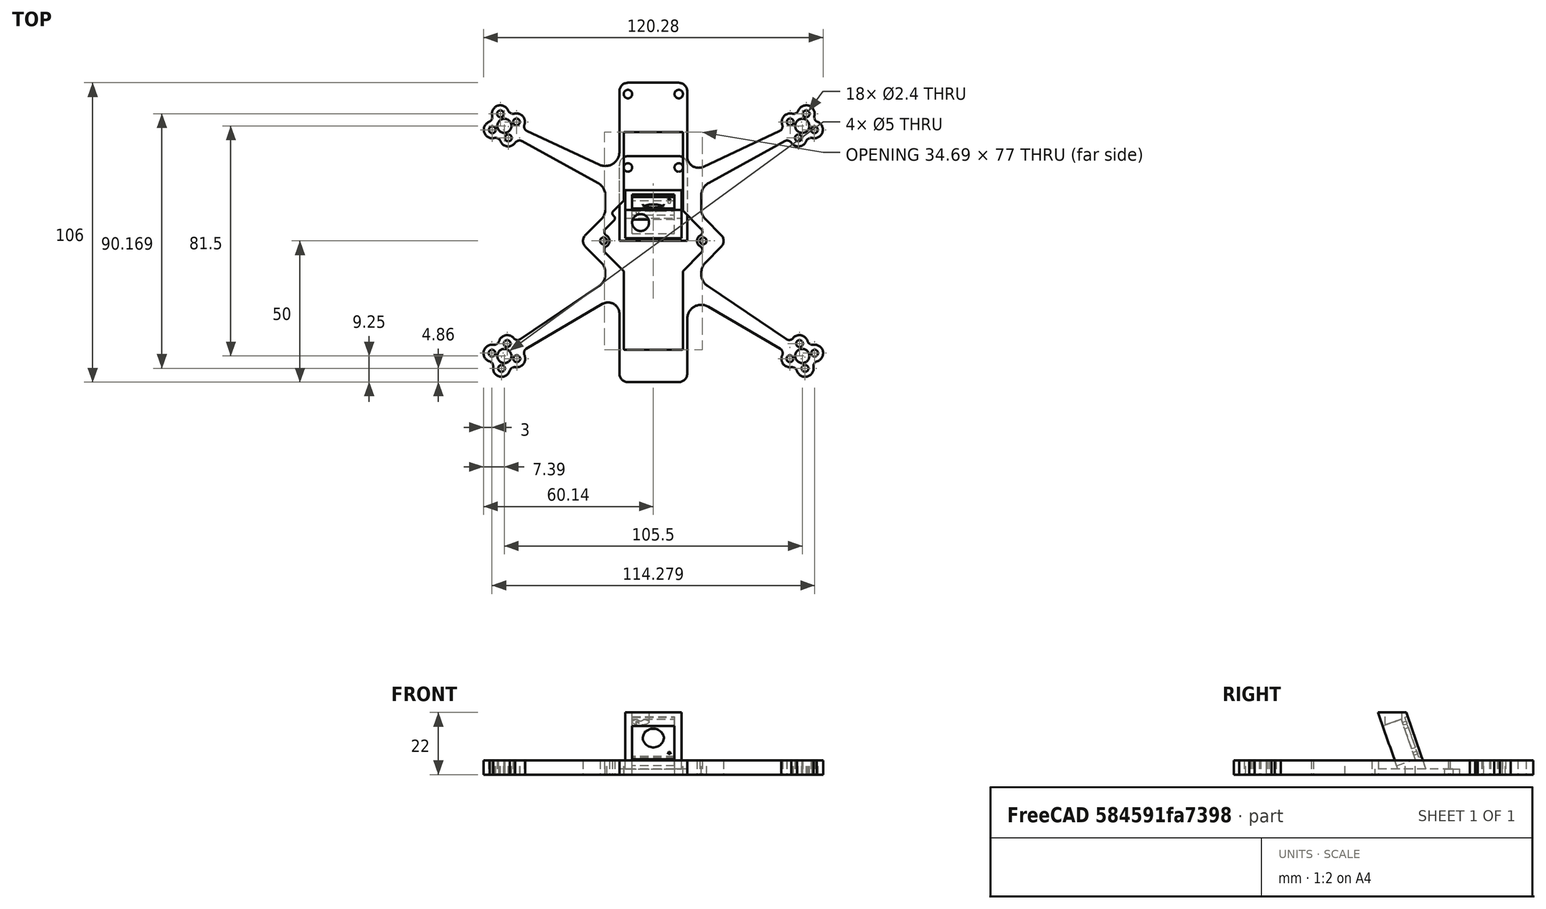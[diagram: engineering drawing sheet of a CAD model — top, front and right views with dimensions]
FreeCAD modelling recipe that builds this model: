
FCSTD DOCUMENT  (FreeCAD 0.19R)
Label: board_outline
License: All rights reserved
LicenseURL: http://en.wikipedia.org/wiki/All_rights_reserved
objects: Sketcher::SketchObject×10, PartDesign::Pocket×5, PartDesign::Pad×2, PartDesign::Body×2, Fem::FemSolverObjectPython×1, Fem::FemMeshObjectPython×1, App::MaterialObjectPython×1, Fem::ConstraintFixed×1, Fem::ConstraintForce×1, Fem::FemAnalysis×1, Spreadsheet::Sheet×1, PartDesign::AdditiveLoft×1
note: 28 computed .brp shape members not serialized (recipe doc carries the construction recipe); baked Part::Feature solids carry a one-line shape summary decoded from their .brp

FEATURE [Sketcher::SketchObject] Sketch  label="Right Half"
  FullyConstrained = true
  MapMode = 5
  Support = -> [XY_Plane]
  expr: Constraints[0] = Spreadsheet.PropDiameter
  sketch-geometry (208):
    g0: Circle CenterX=52.75 CenterY=40.75 CenterZ=0 NormalX=0 NormalY=0 NormalZ=1 AngleXU=0 Radius=38.25
    g1: LineSegment StartX=0 StartY=40.75 StartZ=0 EndX=52.75 EndY=40.75 EndZ=0
    g2: LineSegment StartX=52.75 StartY=40.75 StartZ=0 EndX=52.75 EndY=-40.75 EndZ=0
    g3: LineSegment StartX=52.75 StartY=-40.75 StartZ=0 EndX=0 EndY=-40.75 EndZ=0
    g4: LineSegment StartX=0 StartY=-40.75 StartZ=0 EndX=0 EndY=40.75 EndZ=0
    g5: Circle CenterX=52.75 CenterY=-40.75 CenterZ=0 NormalX=0 NormalY=0 NormalZ=1 AngleXU=0 Radius=38.25
    g6: Circle CenterX=52.75 CenterY=40.75 CenterZ=0 NormalX=0 NormalY=0 NormalZ=1 AngleXU=0 Radius=40.75
    g7: Circle CenterX=52.75 CenterY=-40.75 CenterZ=0 NormalX=0 NormalY=0 NormalZ=1 AngleXU=0 Radius=40.75
    g8: LineSegment StartX=0 StartY=56 StartZ=0 EndX=9 EndY=56 EndZ=0
    g9: LineSegment StartX=9 StartY=-50 StartZ=0 EndX=0 EndY=-50 EndZ=0
    g10: Circle CenterX=52.75 CenterY=-40.75 CenterZ=0 NormalX=0 NormalY=0 NormalZ=1 AngleXU=0 Radius=4.5
    g11: LineSegment StartX=57.1397 StartY=-39.7598 StartZ=0 EndX=51.7598 EndY=-36.3603 EndZ=0
    g12: LineSegment StartX=51.7598 StartY=-36.3603 StartZ=0 EndX=48.3603 EndY=-41.7402 EndZ=0
    g13: LineSegment StartX=48.3603 StartY=-41.7402 StartZ=0 EndX=53.7402 EndY=-45.1397 EndZ=0
    g14: LineSegment StartX=53.7402 StartY=-45.1397 StartZ=0 EndX=57.1397 EndY=-39.7598 EndZ=0
    g15: Circle CenterX=52.75 CenterY=-40.75 CenterZ=0 NormalX=0 NormalY=0 NormalZ=1 AngleXU=0 Radius=4.5
    g16: LineSegment StartX=60.0662 StartY=-39.0997 StartZ=0 EndX=51.0997 EndY=-33.4338 EndZ=0
    g17: LineSegment StartX=51.0997 StartY=-33.4338 StartZ=0 EndX=45.4338 EndY=-42.4003 EndZ=0
    g18: LineSegment StartX=45.4338 StartY=-42.4003 StartZ=0 EndX=54.4003 EndY=-48.0662 EndZ=0
    g19: LineSegment StartX=54.4003 StartY=-48.0662 StartZ=0 EndX=60.0662 EndY=-39.0997 EndZ=0
    g20: Circle CenterX=52.75 CenterY=-40.75 CenterZ=0 NormalX=0 NormalY=0 NormalZ=1 AngleXU=0 Radius=7.5
    g21: LineSegment StartX=57.3995 StartY=-43.688 StartZ=0 EndX=55.688 EndY=-36.1005 EndZ=0
    g22: LineSegment StartX=55.688 StartY=-36.1005 StartZ=0 EndX=48.1005 EndY=-37.812 EndZ=0
    g23: LineSegment StartX=48.1005 StartY=-37.812 StartZ=0 EndX=49.812 EndY=-45.3995 EndZ=0
    g24: LineSegment StartX=49.812 StartY=-45.3995 StartZ=0 EndX=57.3995 EndY=-43.688 EndZ=0
    g25: Circle CenterX=52.75 CenterY=-40.75 CenterZ=0 NormalX=0 NormalY=0 NormalZ=1 AngleXU=0 Radius=5.5
    g26: ArcOfCircle CenterX=51.7598 CenterY=-36.3603 CenterZ=0 NormalX=0 NormalY=0 NormalZ=1 AngleXU=0 Radius=3 StartAngle=0.258897 EndAngle=2.45241
    g27: ArcOfCircle CenterX=57.1397 CenterY=-39.7598 CenterZ=0 NormalX=0 NormalY=0 NormalZ=1 AngleXU=0 Radius=3 StartAngle=4.97129 EndAngle=8.03879
    g28: ArcOfCircle CenterX=53.7402 CenterY=-45.1397 CenterZ=0 NormalX=0 NormalY=0 NormalZ=1 AngleXU=0 Radius=3 StartAngle=3.40049 EndAngle=6.46799
    g29: ArcOfCircle CenterX=48.3603 CenterY=-41.7402 CenterZ=0 NormalX=0 NormalY=0 NormalZ=1 AngleXU=0 Radius=3 StartAngle=2.70369 EndAngle=4.89719
    g30: ArcOfCircle CenterX=58.6676 CenterY=-44.4893 CenterZ=0 NormalX=0 NormalY=0 NormalZ=1 AngleXU=0 Radius=1.98096 StartAngle=1.96444 EndAngle=3.19165
    g31: ArcOfCircle CenterX=56.4893 CenterY=-34.8324 CenterZ=0 NormalX=0 NormalY=0 NormalZ=1 AngleXU=0 Radius=1.98096 StartAngle=3.53523 EndAngle=4.76245
    g32: Circle CenterX=52.75 CenterY=-40.75 CenterZ=0 NormalX=0 NormalY=0 NormalZ=1 AngleXU=0 Radius=7
    g33: Circle CenterX=52.75 CenterY=40.75 CenterZ=0 NormalX=0 NormalY=0 NormalZ=1 AngleXU=0 Radius=4.5
    g34: LineSegment StartX=48.4706 StartY=42.1417 StartZ=0 EndX=51.3583 EndY=36.4706 EndZ=0
    g35: LineSegment StartX=51.3583 StartY=36.4706 StartZ=0 EndX=57.0294 EndY=39.3583 EndZ=0
    g36: LineSegment StartX=57.0294 StartY=39.3583 StartZ=0 EndX=54.1417 EndY=45.0294 EndZ=0
    g37: LineSegment StartX=54.1417 StartY=45.0294 StartZ=0 EndX=48.4706 EndY=42.1417 EndZ=0
    g38: Circle CenterX=52.75 CenterY=40.75 CenterZ=0 NormalX=0 NormalY=0 NormalZ=1 AngleXU=0 Radius=4.5
    g39: LineSegment StartX=45.6177 StartY=43.0695 StartZ=0 EndX=50.4305 EndY=33.6177 EndZ=0
    g40: LineSegment StartX=50.4305 StartY=33.6177 StartZ=0 EndX=59.8823 EndY=38.4305 EndZ=0
    g41: LineSegment StartX=59.8823 StartY=38.4305 StartZ=0 EndX=55.0695 EndY=47.8823 EndZ=0
    g42: LineSegment StartX=55.0695 StartY=47.8823 StartZ=0 EndX=45.6177 EndY=43.0695 EndZ=0
    g43: Circle CenterX=52.75 CenterY=40.75 CenterZ=0 NormalX=0 NormalY=0 NormalZ=1 AngleXU=0 Radius=7.5
    g44: LineSegment StartX=50.2543 StartY=45.6512 StartZ=0 EndX=47.8488 EndY=38.2543 EndZ=0
    g45: LineSegment StartX=47.8488 StartY=38.2543 StartZ=0 EndX=55.2457 EndY=35.8488 EndZ=0
    g46: LineSegment StartX=55.2457 StartY=35.8488 StartZ=0 EndX=57.6512 EndY=43.2457 EndZ=0
    g47: LineSegment StartX=57.6512 StartY=43.2457 StartZ=0 EndX=50.2543 EndY=45.6512 EndZ=0
    g48: Circle CenterX=52.75 CenterY=40.75 CenterZ=0 NormalX=0 NormalY=0 NormalZ=1 AngleXU=0 Radius=5.5
    g49: ArcOfCircle CenterX=51.3583 CenterY=36.4706 CenterZ=0 NormalX=0 NormalY=0 NormalZ=1 AngleXU=0 Radius=3 StartAngle=3.73822 EndAngle=5.93172
    g50: ArcOfCircle CenterX=48.4706 CenterY=42.1417 CenterZ=0 NormalX=0 NormalY=0 NormalZ=1 AngleXU=0 Radius=3 StartAngle=1.29343 EndAngle=3.48693
    g51: ArcOfCircle CenterX=54.1417 CenterY=45.0294 CenterZ=0 NormalX=0 NormalY=0 NormalZ=1 AngleXU=0 Radius=3 StartAngle=6.00582 EndAngle=9.07332
    g52: ArcOfCircle CenterX=57.0294 CenterY=39.3583 CenterZ=0 NormalX=0 NormalY=0 NormalZ=1 AngleXU=0 Radius=3 StartAngle=4.43502 EndAngle=7.50252
    g53: ArcOfCircle CenterX=55.9263 CenterY=34.5121 CenterZ=0 NormalX=0 NormalY=0 NormalZ=1 AngleXU=0 Radius=1.98096 StartAngle=1.42817 EndAngle=2.65539
    g54: ArcOfCircle CenterX=58.9879 CenterY=43.9263 CenterZ=0 NormalX=0 NormalY=0 NormalZ=1 AngleXU=0 Radius=1.98096 StartAngle=2.99897 EndAngle=4.22618
    g55: ArcOfCircle CenterX=49.5737 CenterY=46.9879 CenterZ=0 NormalX=0 NormalY=0 NormalZ=1 AngleXU=0 Radius=1.98096 StartAngle=4.56976 EndAngle=5.79698
    g56: Circle CenterX=52.75 CenterY=40.75 CenterZ=0 NormalX=0 NormalY=0 NormalZ=1 AngleXU=0 Radius=7
    g57: ArcOfCircle CenterX=49.0107 CenterY=-46.6676 CenterZ=0 NormalX=0 NormalY=0 NormalZ=1 AngleXU=0 Radius=1.98096 StartAngle=0.39364 EndAngle=1.62086
    g58: LineSegment StartX=52.75 StartY=40.75 StartZ=0 EndX=12 EndY=20 EndZ=0
    g59: LineSegment StartX=52.75 StartY=-40.75 StartZ=0 EndX=12 EndY=-15 EndZ=0
    g60: LineSegment StartX=-17.65 StartY=0 StartZ=0 EndX=3.6e-15 EndY=-17.65 EndZ=0
    g61: LineSegment StartX=3.6e-15 StartY=-17.65 StartZ=0 EndX=17.65 EndY=0 EndZ=0
    g62: LineSegment StartX=17.65 StartY=0 StartZ=0 EndX=0 EndY=17.65 EndZ=0
    g63: Circle CenterX=0 CenterY=0 CenterZ=0 NormalX=0 NormalY=0 NormalZ=1 AngleXU=0 Radius=17.65
    g64: LineSegment StartX=18.4645 StartY=7.67082 StartZ=0 EndX=24.014 EndY=2.12132 EndZ=0
    g65: LineSegment StartX=24.014 StartY=-2.12132 StartZ=0 EndX=18.4645 EndY=-7.67082 EndZ=0
    g66: ArcOfCircle CenterX=9 CenterY=53 CenterZ=0 NormalX=0 NormalY=0 NormalZ=1 AngleXU=0 Radius=3 StartAngle=1.82596e-08 EndAngle=1.5708
    g67: ArcOfCircle CenterX=9 CenterY=-47 CenterZ=0 NormalX=0 NormalY=0 NormalZ=1 AngleXU=0 Radius=3 StartAngle=4.71239 EndAngle=6.28319
    g68: ArcOfCircle CenterX=21.8926 CenterY=-1.9e-15 CenterZ=0 NormalX=0 NormalY=0 NormalZ=1 AngleXU=0 Radius=3 StartAngle=5.49779 EndAngle=7.06858
    g69: LineSegment StartX=19.2045 StartY=-16.0038 StartZ=0 EndX=47.073 EndY=-34.7968 EndZ=0
    g70: LineSegment StartX=19.5258 StartY=-23.3043 StartZ=0 EndX=44.9296 EndY=-38.1741 EndZ=0
    g71: LineSegment StartX=44.7257 StartY=38.9084 StartZ=0 EndX=17.6946 EndY=26.2662 EndZ=0
    g72: LineSegment StartX=46.5424 StartY=35.3447 StartZ=0 EndX=19.5876 EndY=20.4971 EndZ=0
    g73: LineSegment StartX=-17.65 StartY=0 StartZ=0 EndX=0 EndY=17.65 EndZ=0
    g74: ArcOfCircle CenterX=48.0693 CenterY=-33.3194 CenterZ=0 NormalX=0 NormalY=0 NormalZ=1 AngleXU=0 Radius=1.78198 StartAngle=4.11909 EndAngle=5.594
    g75: ArcOfCircle CenterX=44.0292 CenterY=-39.7123 CenterZ=0 NormalX=0 NormalY=0 NormalZ=1 AngleXU=0 Radius=1.78232 StartAngle=5.84529 EndAngle=7.32441
    g76: ArcOfCircle CenterX=43.9707 CenterY=40.5228 CenterZ=0 NormalX=0 NormalY=0 NormalZ=1 AngleXU=0 Radius=1.78228 StartAngle=5.14985 EndAngle=6.62852
    g77: ArcOfCircle CenterX=47.4023 CenterY=33.7837 CenterZ=0 NormalX=0 NormalY=0 NormalZ=1 AngleXU=0 Radius=1.7822 StartAngle=0.596627 EndAngle=2.07428
    g78: Circle CenterX=51.7598 CenterY=-36.3603 CenterZ=0 NormalX=0 NormalY=0 NormalZ=1 AngleXU=0 Radius=1.2
    g79: Circle CenterX=57.1397 CenterY=-39.7598 CenterZ=0 NormalX=0 NormalY=0 NormalZ=1 AngleXU=0 Radius=1.2
    g80: Circle CenterX=53.7402 CenterY=-45.1397 CenterZ=0 NormalX=0 NormalY=0 NormalZ=1 AngleXU=0 Radius=1.2
    g81: Circle CenterX=48.3603 CenterY=-41.7402 CenterZ=0 NormalX=0 NormalY=0 NormalZ=1 AngleXU=0 Radius=1.2
    g82: Circle CenterX=51.3583 CenterY=36.4706 CenterZ=0 NormalX=0 NormalY=0 NormalZ=1 AngleXU=0 Radius=1.2
    g83: Circle CenterX=57.0294 CenterY=39.3583 CenterZ=0 NormalX=0 NormalY=0 NormalZ=1 AngleXU=0 Radius=1.2
    g84: Circle CenterX=54.1417 CenterY=45.0294 CenterZ=0 NormalX=0 NormalY=0 NormalZ=1 AngleXU=0 Radius=1.2
    g85: Circle CenterX=48.4706 CenterY=42.1417 CenterZ=0 NormalX=0 NormalY=0 NormalZ=1 AngleXU=0 Radius=1.2
    g86: Circle CenterX=52.75 CenterY=-40.75 CenterZ=0 NormalX=0 NormalY=0 NormalZ=1 AngleXU=0 Radius=2.5
    g87: Circle CenterX=52.75 CenterY=40.75 CenterZ=0 NormalX=0 NormalY=0 NormalZ=1 AngleXU=0 Radius=2.5
    g88: LineSegment StartX=12 StartY=-12.943 StartZ=0 EndX=12 EndY=-27.6195 EndZ=0
    g89: LineSegment StartX=12 StartY=-27.6195 StartZ=0 EndX=12 EndY=-47 EndZ=0
    g90: LineSegment StartX=12 StartY=53 StartZ=0 EndX=12 EndY=29.8895 EndZ=0
    g91: ArcOfCircle CenterX=16 CenterY=29.8895 CenterZ=0 NormalX=0 NormalY=0 NormalZ=1 AngleXU=0 Radius=4 StartAngle=3.14159 EndAngle=5.14985
    g92: ArcOfCircle CenterX=17 CenterY=-27.6195 CenterZ=0 NormalX=0 NormalY=0 NormalZ=1 AngleXU=0 Radius=5 StartAngle=1.04123 EndAngle=3.14159
    g93: LineSegment StartX=19.2045 StartY=-16.0038 StartZ=0 EndX=17.6019 EndY=-18.5399 EndZ=0
    g94: LineSegment StartX=19.5258 StartY=-23.3043 StartZ=0 EndX=21.1284 EndY=-20.7682 EndZ=0
    g95: LineSegment StartX=18.2263 StartY=23.1705 StartZ=0 EndX=19.5876 EndY=20.4971 EndZ=0
    g96: LineSegment StartX=19.0559 StartY=23.5929 StartZ=0 EndX=17.6946 EndY=26.2662 EndZ=0
    g97: Circle CenterX=-52.75 CenterY=-40.75 CenterZ=0 NormalX=0 NormalY=0 NormalZ=1 AngleXU=0 Radius=38.25
    g98: LineSegment StartX=0 StartY=-40.75 StartZ=0 EndX=-52.75 EndY=-40.75 EndZ=0
    g99: LineSegment StartX=-52.75 StartY=-40.75 StartZ=0 EndX=-52.75 EndY=40.75 EndZ=0
    g100: LineSegment StartX=-52.75 StartY=40.75 StartZ=0 EndX=0 EndY=40.75 EndZ=0
    g101: LineSegment StartX=0 StartY=40.75 StartZ=0 EndX=0 EndY=-40.75 EndZ=0
    g102: Circle CenterX=-52.75 CenterY=40.75 CenterZ=0 NormalX=0 NormalY=0 NormalZ=1 AngleXU=0 Radius=38.25
    g103: Circle CenterX=-52.75 CenterY=-40.75 CenterZ=0 NormalX=0 NormalY=0 NormalZ=1 AngleXU=0 Radius=40.75
    g104: Circle CenterX=-52.75 CenterY=40.75 CenterZ=0 NormalX=0 NormalY=0 NormalZ=1 AngleXU=0 Radius=40.75
    g105: LineSegment StartX=0 StartY=-50 StartZ=0 EndX=-8.99997 EndY=-50 EndZ=0
    g106: LineSegment StartX=-9 StartY=56 StartZ=0 EndX=0 EndY=56 EndZ=0
    g107: Circle CenterX=-52.75 CenterY=40.75 CenterZ=0 NormalX=0 NormalY=0 NormalZ=1 AngleXU=0 Radius=4.5
    g108: LineSegment StartX=-57.0294 StartY=39.3583 StartZ=0 EndX=-51.3583 EndY=36.4706 EndZ=0
    g109: LineSegment StartX=-51.3583 StartY=36.4706 StartZ=0 EndX=-48.4706 EndY=42.1417 EndZ=0
    g110: LineSegment StartX=-48.4706 StartY=42.1417 StartZ=0 EndX=-54.1417 EndY=45.0294 EndZ=0
    g111: LineSegment StartX=-54.1417 StartY=45.0294 StartZ=0 EndX=-57.0294 EndY=39.3583 EndZ=0
    g112: Circle CenterX=-52.75 CenterY=40.75 CenterZ=0 NormalX=0 NormalY=0 NormalZ=1 AngleXU=0 Radius=4.5
    g113: LineSegment StartX=-59.8823 StartY=38.4305 StartZ=0 EndX=-50.4305 EndY=33.6177 EndZ=0
    g114: LineSegment StartX=-50.4305 StartY=33.6177 StartZ=0 EndX=-45.6177 EndY=43.0695 EndZ=0
    g115: LineSegment StartX=-45.6177 StartY=43.0695 StartZ=0 EndX=-55.0695 EndY=47.8823 EndZ=0
    g116: LineSegment StartX=-55.0695 StartY=47.8823 StartZ=0 EndX=-59.8823 EndY=38.4305 EndZ=0
    g117: Circle CenterX=-52.75 CenterY=40.75 CenterZ=0 NormalX=0 NormalY=0 NormalZ=1 AngleXU=0 Radius=7.5
    g118: LineSegment StartX=-57.6512 StartY=43.2457 StartZ=0 EndX=-55.2457 EndY=35.8488 EndZ=0
    g119: LineSegment StartX=-55.2457 StartY=35.8488 StartZ=0 EndX=-47.8488 EndY=38.2543 EndZ=0
    g120: LineSegment StartX=-47.8488 StartY=38.2543 StartZ=0 EndX=-50.2543 EndY=45.6512 EndZ=0
    g121: LineSegment StartX=-50.2543 StartY=45.6512 StartZ=0 EndX=-57.6512 EndY=43.2457 EndZ=0
    g122: Circle CenterX=-52.75 CenterY=40.75 CenterZ=0 NormalX=0 NormalY=0 NormalZ=1 AngleXU=0 Radius=5.5
    g123: ArcOfCircle CenterX=-51.3583 CenterY=36.4706 CenterZ=0 NormalX=0 NormalY=0 NormalZ=1 AngleXU=0 Radius=3 StartAngle=3.49305 EndAngle=5.68656
    g124: ArcOfCircle CenterX=-57.0294 CenterY=39.3583 CenterZ=0 NormalX=0 NormalY=0 NormalZ=1 AngleXU=0 Radius=3 StartAngle=1.92226 EndAngle=4.98976
    g125: ArcOfCircle CenterX=-54.1417 CenterY=45.0294 CenterZ=0 NormalX=0 NormalY=0 NormalZ=1 AngleXU=0 Radius=3 StartAngle=0.351461 EndAngle=3.41896
    g126: ArcOfCircle CenterX=-48.4706 CenterY=42.1417 CenterZ=0 NormalX=0 NormalY=0 NormalZ=1 AngleXU=0 Radius=3 StartAngle=5.93786 EndAngle=8.13135
    g127: ArcOfCircle CenterX=-58.9879 CenterY=43.9263 CenterZ=0 NormalX=0 NormalY=0 NormalZ=1 AngleXU=0 Radius=1.98096 StartAngle=5.19859 EndAngle=6.42581
    g128: ArcOfCircle CenterX=-55.9263 CenterY=34.5121 CenterZ=0 NormalX=0 NormalY=0 NormalZ=1 AngleXU=0 Radius=1.98096 StartAngle=0.486205 EndAngle=1.71342
    g129: Circle CenterX=-52.75 CenterY=40.75 CenterZ=0 NormalX=0 NormalY=0 NormalZ=1 AngleXU=0 Radius=7
    g130: Circle CenterX=-52.75 CenterY=-40.75 CenterZ=0 NormalX=0 NormalY=0 NormalZ=1 AngleXU=0 Radius=4.5
    g131: LineSegment StartX=-48.3603 StartY=-41.7402 StartZ=0 EndX=-51.7598 EndY=-36.3603 EndZ=0
    g132: LineSegment StartX=-51.7598 StartY=-36.3603 StartZ=0 EndX=-57.1397 EndY=-39.7598 EndZ=0
    g133: LineSegment StartX=-57.1397 StartY=-39.7598 StartZ=0 EndX=-53.7401 EndY=-45.1397 EndZ=0
    g134: LineSegment StartX=-53.7401 StartY=-45.1397 StartZ=0 EndX=-48.3603 EndY=-41.7402 EndZ=0
    g135: Circle CenterX=-52.75 CenterY=-40.75 CenterZ=0 NormalX=0 NormalY=0 NormalZ=1 AngleXU=0 Radius=4.5
    g136: LineSegment StartX=-45.4338 StartY=-42.4003 StartZ=0 EndX=-51.0997 EndY=-33.4338 EndZ=0
    g137: LineSegment StartX=-51.0997 StartY=-33.4338 StartZ=0 EndX=-60.0662 EndY=-39.0997 EndZ=0
    g138: LineSegment StartX=-60.0662 StartY=-39.0997 StartZ=0 EndX=-54.4002 EndY=-48.0662 EndZ=0
    g139: LineSegment StartX=-54.4002 StartY=-48.0662 StartZ=0 EndX=-45.4338 EndY=-42.4003 EndZ=0
    g140: Circle CenterX=-52.75 CenterY=-40.75 CenterZ=0 NormalX=0 NormalY=0 NormalZ=1 AngleXU=0 Radius=7.5
    g141: LineSegment StartX=-49.8119 StartY=-45.3995 StartZ=0 EndX=-48.1005 EndY=-37.812 EndZ=0
    g142: LineSegment StartX=-48.1005 StartY=-37.812 StartZ=0 EndX=-55.688 EndY=-36.1005 EndZ=0
    g143: LineSegment StartX=-55.688 StartY=-36.1005 StartZ=0 EndX=-57.3995 EndY=-43.688 EndZ=0
    g144: LineSegment StartX=-57.3995 StartY=-43.688 StartZ=0 EndX=-49.8119 EndY=-45.3995 EndZ=0
    g145: Circle CenterX=-52.75 CenterY=-40.75 CenterZ=0 NormalX=0 NormalY=0 NormalZ=1 AngleXU=0 Radius=5.5
    g146: ArcOfCircle CenterX=-51.7598 CenterY=-36.3603 CenterZ=0 NormalX=0 NormalY=0 NormalZ=1 AngleXU=0 Radius=3 StartAngle=0.689184 EndAngle=2.8827
    g147: ArcOfCircle CenterX=-48.3603 CenterY=-41.7402 CenterZ=0 NormalX=0 NormalY=0 NormalZ=1 AngleXU=0 Radius=3 StartAngle=4.52758 EndAngle=6.72109
    g148: ArcOfCircle CenterX=-53.7401 CenterY=-45.1397 CenterZ=0 NormalX=0 NormalY=0 NormalZ=1 AngleXU=0 Radius=3 StartAngle=2.95679 EndAngle=6.02429
    g149: ArcOfCircle CenterX=-57.1397 CenterY=-39.7598 CenterZ=0 NormalX=0 NormalY=0 NormalZ=1 AngleXU=0 Radius=3 StartAngle=1.38599 EndAngle=4.45349
    g150: ArcOfCircle CenterX=-56.4893 CenterY=-34.8324 CenterZ=0 NormalX=0 NormalY=0 NormalZ=1 AngleXU=0 Radius=1.98096 StartAngle=4.66233 EndAngle=5.88955
    g151: ArcOfCircle CenterX=-58.6675 CenterY=-44.4893 CenterZ=0 NormalX=0 NormalY=0 NormalZ=1 AngleXU=0 Radius=1.98096 StartAngle=6.23312 EndAngle=7.46034
    g152: ArcOfCircle CenterX=-49.0107 CenterY=-46.6676 CenterZ=0 NormalX=0 NormalY=0 NormalZ=1 AngleXU=0 Radius=1.98096 StartAngle=1.52073 EndAngle=2.74795
    g153: Circle CenterX=-52.75 CenterY=-40.75 CenterZ=0 NormalX=0 NormalY=0 NormalZ=1 AngleXU=0 Radius=7
    g154: ArcOfCircle CenterX=-49.5737 CenterY=46.9879 CenterZ=0 NormalX=0 NormalY=0 NormalZ=1 AngleXU=0 Radius=1.98096 StartAngle=3.6278 EndAngle=4.85502
    g155: LineSegment StartX=-52.75 StartY=-40.75 StartZ=0 EndX=-12 EndY=-15 EndZ=0
    g156: LineSegment StartX=-52.75 StartY=40.75 StartZ=0 EndX=-12 EndY=20 EndZ=0
    g157: LineSegment StartX=-24.014 StartY=2.12132 StartZ=0 EndX=-18.4645 EndY=7.67082 EndZ=0
    g158: ArcOfCircle CenterX=-8.99997 CenterY=-47 CenterZ=0 NormalX=0 NormalY=0 NormalZ=1 AngleXU=0 Radius=3 StartAngle=3.14159 EndAngle=4.71239
    g159: ArcOfCircle CenterX=-9 CenterY=53 CenterZ=0 NormalX=0 NormalY=0 NormalZ=1 AngleXU=0 Radius=3 StartAngle=1.5708 EndAngle=3.14159
    g160: ArcOfCircle CenterX=-21.8926 CenterY=6e-16 CenterZ=0 NormalX=0 NormalY=0 NormalZ=1 AngleXU=0 Radius=3 StartAngle=2.35619 EndAngle=3.92699
    g161: LineSegment StartX=-19.5876 StartY=20.4971 StartZ=0 EndX=-46.5424 EndY=35.3447 EndZ=0
    g162: LineSegment StartX=-19.1097 StartY=26.9868 StartZ=0 EndX=-44.7226 EndY=38.9068 EndZ=0
    g163: LineSegment StartX=-44.9326 StartY=-38.176 StartZ=0 EndX=-18.0273 EndY=-22.3574 EndZ=0
    g164: LineSegment StartX=-47.0729 StartY=-34.7968 StartZ=0 EndX=-19.2045 EndY=-16.0038 EndZ=0
    g165: ArcOfCircle CenterX=-47.4023 CenterY=33.7837 CenterZ=0 NormalX=0 NormalY=0 NormalZ=1 AngleXU=0 Radius=1.7822 StartAngle=1.06731 EndAngle=2.54497
    g166: ArcOfCircle CenterX=-43.9705 CenterY=40.5228 CenterZ=0 NormalX=0 NormalY=0 NormalZ=1 AngleXU=0 Radius=1.78244 StartAngle=2.79626 EndAngle=4.27681
    g167: ArcOfCircle CenterX=-44.0293 CenterY=-39.7123 CenterZ=0 NormalX=0 NormalY=0 NormalZ=1 AngleXU=0 Radius=1.78216 StartAngle=2.1023 EndAngle=3.5795
    g168: ArcOfCircle CenterX=-48.0692 CenterY=-33.3194 CenterZ=0 NormalX=0 NormalY=0 NormalZ=1 AngleXU=0 Radius=1.78198 StartAngle=3.83078 EndAngle=5.30569
    g169: Circle CenterX=-51.3583 CenterY=36.4706 CenterZ=0 NormalX=0 NormalY=0 NormalZ=1 AngleXU=0 Radius=1.2
    g170: Circle CenterX=-57.0294 CenterY=39.3583 CenterZ=0 NormalX=0 NormalY=0 NormalZ=1 AngleXU=0 Radius=1.2
    g171: Circle CenterX=-54.1417 CenterY=45.0294 CenterZ=0 NormalX=0 NormalY=0 NormalZ=1 AngleXU=0 Radius=1.2
    g172: Circle CenterX=-48.4706 CenterY=42.1417 CenterZ=0 NormalX=0 NormalY=0 NormalZ=1 AngleXU=0 Radius=1.2
    g173: Circle CenterX=-51.7598 CenterY=-36.3603 CenterZ=0 NormalX=0 NormalY=0 NormalZ=1 AngleXU=0 Radius=1.2
    g174: Circle CenterX=-57.1397 CenterY=-39.7598 CenterZ=0 NormalX=0 NormalY=0 NormalZ=1 AngleXU=0 Radius=1.2
    g175: Circle CenterX=-53.7401 CenterY=-45.1397 CenterZ=0 NormalX=0 NormalY=0 NormalZ=1 AngleXU=0 Radius=1.2
    g176: Circle CenterX=-48.3603 CenterY=-41.7402 CenterZ=0 NormalX=0 NormalY=0 NormalZ=1 AngleXU=0 Radius=1.2
    g177: Circle CenterX=-52.75 CenterY=40.75 CenterZ=0 NormalX=0 NormalY=0 NormalZ=1 AngleXU=0 Radius=2.5
    g178: Circle CenterX=-52.75 CenterY=-40.75 CenterZ=0 NormalX=0 NormalY=0 NormalZ=1 AngleXU=0 Radius=2.5
    g179: LineSegment StartX=-12 StartY=12.943 StartZ=0 EndX=-12 EndY=31.5199 EndZ=0
    g180: LineSegment StartX=-12 StartY=31.5199 StartZ=0 EndX=-12 EndY=53 EndZ=0
    g181: LineSegment StartX=-12 StartY=-47 StartZ=0 EndX=-12 EndY=-25.8056 EndZ=0
    g182: LineSegment StartX=-12 StartY=-25.8056 StartZ=0 EndX=-12 EndY=-12.9431 EndZ=0
    g183: ArcOfCircle CenterX=-16 CenterY=-25.8056 CenterZ=0 NormalX=0 NormalY=0 NormalZ=1 AngleXU=0 Radius=4 StartAngle=0 EndAngle=2.1023
    g184: ArcOfCircle CenterX=-17 CenterY=31.5199 CenterZ=0 NormalX=0 NormalY=0 NormalZ=1 AngleXU=0 Radius=5 StartAngle=4.27681 EndAngle=6.28319
    g185: LineSegment StartX=-19.5876 StartY=20.4971 StartZ=0 EndX=-18.2263 EndY=23.1705 EndZ=0
    g186: LineSegment StartX=-19.1097 StartY=26.9868 StartZ=0 EndX=-20.471 EndY=24.3134 EndZ=0
    g187: LineSegment StartX=-17.6019 StartY=-18.5399 StartZ=0 EndX=-19.2045 EndY=-16.0038 EndZ=0
    g188: LineSegment StartX=-19.6298 StartY=-19.8213 StartZ=0 EndX=-18.0273 EndY=-22.3574 EndZ=0
    g189: Circle CenterX=-17.65 CenterY=0 CenterZ=0 NormalX=0 NormalY=0 NormalZ=1 AngleXU=0 Radius=1.2
    g190: Circle CenterX=17.65 CenterY=0 CenterZ=0 NormalX=0 NormalY=0 NormalZ=1 AngleXU=0 Radius=1.2
    g191: Circle CenterX=0 CenterY=17.65 CenterZ=0 NormalX=0 NormalY=0 NormalZ=1 AngleXU=0 Radius=1.2
    g192: Circle CenterX=3.6e-15 CenterY=-17.65 CenterZ=0 NormalX=0 NormalY=0 NormalZ=1 AngleXU=0 Radius=1.2
    g193: ArcOfCircle CenterX=22 CenterY=16.1176 CenterZ=0 NormalX=0 NormalY=0 NormalZ=1 AngleXU=0 Radius=5 StartAngle=2.07428 EndAngle=3.14159
    g194: LineSegment StartX=17 StartY=11.2063 StartZ=0 EndX=17 EndY=16.1176 EndZ=0
    g195: ArcOfCircle CenterX=22 CenterY=11.2063 CenterZ=0 NormalX=0 NormalY=0 NormalZ=1 AngleXU=0 Radius=5 StartAngle=3.14159 EndAngle=3.92699
    g196: LineSegment StartX=-17 StartY=-11.2063 StartZ=0 EndX=-17 EndY=-11.8583 EndZ=0
    g197: LineSegment StartX=17 StartY=-11.2063 StartZ=0 EndX=17 EndY=-11.8583 EndZ=0
    g198: ArcOfCircle CenterX=22 CenterY=-11.2063 CenterZ=0 NormalX=0 NormalY=0 NormalZ=1 AngleXU=0 Radius=5 StartAngle=2.35619 EndAngle=3.14159
    g199: ArcOfCircle CenterX=22 CenterY=-11.8583 CenterZ=0 NormalX=0 NormalY=0 NormalZ=1 AngleXU=0 Radius=5 StartAngle=3.14159 EndAngle=4.11909
    g200: ArcOfCircle CenterX=-22 CenterY=-11.8583 CenterZ=0 NormalX=0 NormalY=0 NormalZ=1 AngleXU=0 Radius=5 StartAngle=5.30569 EndAngle=6.28319
    g201: LineSegment StartX=-17 StartY=16.1176 StartZ=0 EndX=-17 EndY=11.2063 EndZ=0
    g202: ArcOfCircle CenterX=-22 CenterY=16.1176 CenterZ=0 NormalX=0 NormalY=0 NormalZ=1 AngleXU=0 Radius=5 StartAngle=0 EndAngle=1.06731
    g203: ArcOfCircle CenterX=-22 CenterY=11.2063 CenterZ=0 NormalX=0 NormalY=0 NormalZ=1 AngleXU=0 Radius=5 StartAngle=5.49779 EndAngle=6.28319
    g204: LineSegment StartX=-24.014 StartY=-2.12132 StartZ=0 EndX=-18.4645 EndY=-7.67082 EndZ=0
    g205: ArcOfCircle CenterX=-22 CenterY=-11.2063 CenterZ=0 NormalX=0 NormalY=0 NormalZ=1 AngleXU=0 Radius=5 StartAngle=6.28319 EndAngle=7.06858
    g206: Circle CenterX=9 CenterY=52 CenterZ=0 NormalX=0 NormalY=0 NormalZ=1 AngleXU=0 Radius=1.5
    g207: Circle CenterX=-9 CenterY=52 CenterZ=0 NormalX=0 NormalY=0 NormalZ=1 AngleXU=0 Radius=1.5
  constraints (563):
    c: Diameter(g0) = 76.5
    c: Horizontal(g1)
    c: Coincident(g1,g2)
    c: Coincident(g2,g3)
    c: Horizontal(g3)
    c: Coincident(g3,g4)
    c: Coincident(g1,g4)
    c: Coincident(g0,g1)
    c: Equal(g0,g5) = 76.5
    c: Coincident(g5,g2)
    c: PointOnObject(g3,g-2)
    c: PointOnObject(g1,g-2)
    c: Tangent(g6,g-1)
    c: Diameter(g6) = 81.5
    c: Coincident(g6,g0)
    c: Equal(g6,g7) = 80
    c: Coincident(g7,g2)
    c: Tangent(g6,g7)
    c: PointOnObject(g8,g-2)
    c: Horizontal(g8)
    c: Horizontal(g9)
    c: PointOnObject(g9,g-2)
    c: DistanceY(g-1,g8) = 56
    c: DistanceY(g9,g-1) = 50
    c: Diameter(g10) = 9
    c: Coincident(g11,g12)
    c: Coincident(g12,g13)
    c: Coincident(g13,g14)
    c: Coincident(g14,g11)
    c: Equal(g11,g12)
    c: Equal(g11,g13)
    c: Equal(g11,g14)
    c: PointOnObject(g11,g15)
    c: PointOnObject(g12,g15)
    c: PointOnObject(g13,g15)
    c: PointOnObject(g14,g15)
    c: Coincident(g15,g10)
    c: PointOnObject(g11,g10)
    c: Coincident(g16,g17)
    c: Coincident(g17,g18)
    c: Coincident(g18,g19)
    c: Coincident(g19,g16)
    c: Equal(g16,g17)
    c: Equal(g16,g18)
    c: Equal(g16,g19)
    c: PointOnObject(g16,g20)
    c: PointOnObject(g17,g20)
    c: PointOnObject(g18,g20)
    c: PointOnObject(g19,g20)
    c: Coincident(g20,g10)
    c: Parallel(g14,g19)
    c: Distance(g10,g16) = 7.5
    c: Coincident(g21,g22)
    c: Coincident(g22,g23)
    c: Coincident(g23,g24)
    c: Coincident(g24,g21)
    c: Equal(g21,g22)
    c: Equal(g21,g23)
    c: Equal(g21,g24)
    c: PointOnObject(g21,g25)
    c: PointOnObject(g22,g25)
    c: PointOnObject(g23,g25)
    c: PointOnObject(g24,g25)
    c: Coincident(g25,g10)
    c: Angle(g14,g21) = 0.785398
    c: Distance(g23,g10) = 5.5
    c: Coincident(g26,g11)
    c: PointOnObject(g16,g26)
    c: PointOnObject(g26,g25)
    c: Coincident(g27,g11)
    c: Coincident(g28,g13)
    c: Coincident(g29,g12)
    c: PointOnObject(g29,g25)
    c: PointOnObject(g27,g25)
    c: PointOnObject(g27,g25)
    c: PointOnObject(g28,g25)
    c: PointOnObject(g28,g25)
    c: PointOnObject(g17,g29)
    c: PointOnObject(g18,g28)
    c: PointOnObject(g16,g27)
    c: Coincident(g31,g26)
    c: Coincident(g31,g27)
    c: Coincident(g27,g30)
    c: Coincident(g30,g28)
    c: Radius(g32) = 7
    c: Coincident(g32,g10)
    c: PointOnObject(g30,g32)
    c: PointOnObject(g31,g32)
    c: Equal(g10,g33) = 9
    c: Coincident(g34,g35)
    c: Coincident(g35,g36)
    c: Coincident(g36,g37)
    c: Coincident(g37,g34)
    c: Equal(g34,g35)
    c: Equal(g34,g36)
    c: Equal(g34,g37)
    c: PointOnObject(g34,g38)
    c: PointOnObject(g35,g38)
    c: PointOnObject(g36,g38)
    c: PointOnObject(g37,g38)
    c: Coincident(g38,g33)
    c: PointOnObject(g34,g33)
    c: Coincident(g39,g40)
    c: Coincident(g40,g41)
    c: Coincident(g41,g42)
    c: Coincident(g42,g39)
    c: Equal(g39,g40)
    c: Equal(g39,g41)
    c: Equal(g39,g42)
    c: PointOnObject(g39,g43)
    c: PointOnObject(g40,g43)
    c: PointOnObject(g41,g43)
    c: PointOnObject(g42,g43)
    c: Coincident(g43,g33)
    c: Parallel(g37,g42)
    c: Distance(g33,g39) = 7.5
    c: Coincident(g44,g45)
    c: Coincident(g45,g46)
    c: Coincident(g46,g47)
    c: Coincident(g47,g44)
    c: Equal(g44,g45)
    c: Equal(g44,g46)
    c: Equal(g44,g47)
    c: PointOnObject(g44,g48)
    c: PointOnObject(g45,g48)
    c: PointOnObject(g46,g48)
    c: PointOnObject(g47,g48)
    c: Coincident(g48,g33)
    c: Angle(g37,g44) = 0.785398
    c: Distance(g46,g33) = 5.5
    c: Coincident(g49,g34)
    c: PointOnObject(g49,g48)
    c: PointOnObject(g39,g49)
    c: Coincident(g50,g34)
    c: Coincident(g51,g36)
    c: Coincident(g52,g35)
    c: PointOnObject(g52,g48)
    c: PointOnObject(g52,g48)
    c: PointOnObject(g50,g48)
    c: PointOnObject(g51,g48)
    c: PointOnObject(g51,g48)
    c: PointOnObject(g40,g52)
    c: PointOnObject(g41,g51)
    c: PointOnObject(g39,g50)
    c: Coincident(g53,g49)
    c: Coincident(g52,g53)
    c: Coincident(g50,g55)
    c: Coincident(g55,g51)
    c: Coincident(g54,g51)
    c: Coincident(g54,g52)
    c: Equal(g32,g56) = 6.5
    c: Coincident(g56,g33)
    c: PointOnObject(g55,g56)
    c: PointOnObject(g54,g56)
    c: PointOnObject(g53,g56)
    c: Coincident(g33,g0)
    c: Coincident(g10,g2)
    c: Coincident(g57,g29)
    c: Coincident(g57,g28)
    c: PointOnObject(g57,g32)
    c: Coincident(g58,g0)
    c: Perpendicular(g39,g58)
    c: Coincident(g59,g2)
    c: DistanceY(g-1,g58) = 20
    c: DistanceY(g59,g-1) = 15
    c: Coincident(g61,g62)
    c: PointOnObject(g61,g63)
    c: PointOnObject(g62,g63)
    c: Coincident(g63,g-1)
    c: Diameter(g63) = 35.3
    c: Parallel(g64,g62)
    c: Parallel(g65,g61)
    c: Tangent(g8,g66) = 1.5708
    c: Tangent(g9,g67) = 1.5708
    c: Tangent(g64,g68) = 1.5708
    c: Tangent(g65,g68) = 1.5708
    c: Radius(g66) = 3
    c: Radius(g68) = 3
    c: Radius(g67) = 3
    c: Coincident(g73,g62)
    c: Coincident(g73,g60)
    c: PointOnObject(g60,g63)
    c: Equal(g73,g61)
    c: Equal(g60,g62)
    c: PointOnObject(g60,g-1)
    c: PointOnObject(g62,g4)
    c: Coincident(g61,g60)
    c: PointOnObject(g60,g63)
    c: Tangent(g69,g74) = -1.5708
    c: Tangent(g26,g74) = 1.5708
    c: Tangent(g29,g75) = 1.5708
    c: Tangent(g70,g75) = 1.5708
    c: Tangent(g74,g32)
    c: Tangent(g75,g32)
    c: Tangent(g71,g76) = 1.5708
    c: Tangent(g50,g76) = 1.5708
    c: Tangent(g72,g77) = -1.5708
    c: Tangent(g49,g77) = 1.5708
    c: Tangent(g77,g56)
    c: Tangent(g76,g56)
    c: Distance(g72,g58) = 2
    c: Distance(g71,g58) = 2
    c: Diameter(g78) = 2.4  'M2-clear'
    c: Coincident(g78,g26)
    c: Equal(g78,g79) = 2.4  'M2-clear'
    c: Coincident(g79,g27)
    c: Equal(g78,g80) = 2.4  'M2-clear'
    c: Coincident(g80,g28)
    c: Equal(g78,g81) = 2.4  'M2-clear'
    c: Coincident(g81,g29)
    c: Distance(g70,g59) = 2
    c: Distance(g69,g59) = 2
    c: Equal(g78,g82) = 2.4  'M2-clear'
    c: Coincident(g82,g49)
    c: Equal(g78,g83) = 2.4  'M2-clear'
    c: Coincident(g83,g52)
    c: Equal(g78,g84) = 2.4  'M2-clear'
    c: Coincident(g84,g51)
    c: Equal(g78,g85) = 2.4  'M2-clear'
    c: Coincident(g85,g50)
    c: Coincident(g86,g2)
    c: Diameter(g86) = 5
    c: Equal(g86,g87) = 5
    c: Coincident(g87,g0)
    c: Vertical(g88)
    c: Coincident(g89,g67)
    c: Vertical(g89)
    c: DistanceX(g3,g59) = 12
    c: PointOnObject(g59,g88)
    c: Coincident(g90,g66)
    c: Vertical(g90)
    c: Tangent(g90,g6)
    c: DistanceX(g1,g58) = 12
    c: Tangent(g7,g89)
    c: Tangent(g89,g67)
    c: Tangent(g66,g90)
    c: Tangent(g71,g91) = 1.5708
    c: Tangent(g90,g91) = -1.5708
    c: Tangent(g70,g92) = 1.5708
    c: Tangent(g89,g92) = -1.5708
    c: Coincident(g88,g89)
    c: Radius(g91) = 4
    c: Radius(g92) = 5
    c: Perpendicular(g17,g59)
    c: PointOnObject(g93,g59)
    c: PointOnObject(g94,g59)
    c: Perpendicular(g59,g93)
    c: Perpendicular(g59,g94)
    c: Coincident(g94,g70)
    c: Distance(g93) = 3
    c: Distance(g94) = 3
    c: Perpendicular(g58,g96)
    c: Perpendicular(g58,g95)
    c: PointOnObject(g95,g58)
    c: PointOnObject(g96,g58)
    c: Coincident(g96,g71)
    c: Coincident(g95,g72)
    c: Distance(g96) = 3
    c: Distance(g95) = 3
    c: Diameter(g97) = 76.5
    c: Horizontal(g98)
    c: Coincident(g98,g99)
    c: Coincident(g99,g100)
    c: Horizontal(g100)
    c: Coincident(g100,g101)
    c: Coincident(g98,g101)
    c: Coincident(g97,g98)
    c: Equal(g97,g102) = 76.5
    c: Coincident(g102,g99)
    c: Diameter(g103) = 81.5
    c: Coincident(g103,g97)
    c: Equal(g103,g104) = 80
    c: Coincident(g104,g99)
    c: Tangent(g103,g104)
    c: Horizontal(g105)
    c: Horizontal(g106)
    c: Diameter(g107) = 9
    c: Coincident(g108,g109)
    c: Coincident(g109,g110)
    c: Coincident(g110,g111)
    c: Coincident(g111,g108)
    c: Equal(g108,g109)
    c: Equal(g108,g110)
    c: Equal(g108,g111)
    c: PointOnObject(g108,g112)
    c: PointOnObject(g109,g112)
    c: PointOnObject(g110,g112)
    c: PointOnObject(g111,g112)
    c: Coincident(g112,g107)
    c: PointOnObject(g108,g107)
    c: Coincident(g113,g114)
    c: Coincident(g114,g115)
    c: Coincident(g115,g116)
    c: Coincident(g116,g113)
    c: Equal(g113,g114)
    c: Equal(g113,g115)
    c: Equal(g113,g116)
    c: PointOnObject(g113,g117)
    c: PointOnObject(g114,g117)
    c: PointOnObject(g115,g117)
    c: PointOnObject(g116,g117)
    c: Coincident(g117,g107)
    c: Parallel(g111,g116)
    c: Distance(g107,g113) = 7.5
    c: Coincident(g118,g119)
    c: Coincident(g119,g120)
    c: Coincident(g120,g121)
    c: Coincident(g121,g118)
    c: Equal(g118,g119)
    c: Equal(g118,g120)
    c: Equal(g118,g121)
    c: PointOnObject(g118,g122)
    c: PointOnObject(g119,g122)
    c: PointOnObject(g120,g122)
    c: PointOnObject(g121,g122)
    c: Coincident(g122,g107)
    c: Angle(g111,g118) = 0.785398
    c: Distance(g120,g107) = 5.5
    c: Coincident(g123,g108)
    c: PointOnObject(g113,g123)
    c: PointOnObject(g123,g122)
    c: Coincident(g124,g108)
    c: Coincident(g125,g110)
    c: Coincident(g126,g109)
    c: PointOnObject(g126,g122)
    c: PointOnObject(g124,g122)
    c: PointOnObject(g124,g122)
    c: PointOnObject(g125,g122)
    c: PointOnObject(g125,g122)
    c: PointOnObject(g114,g126)
    c: PointOnObject(g115,g125)
    c: PointOnObject(g113,g124)
    c: Coincident(g128,g123)
    c: Coincident(g128,g124)
    c: Coincident(g124,g127)
    c: Coincident(g127,g125)
    c: Radius(g129) = 7
    c: Coincident(g129,g107)
    c: PointOnObject(g127,g129)
    c: PointOnObject(g128,g129)
    c: Equal(g107,g130) = 9
    c: Coincident(g131,g132)
    c: Coincident(g132,g133)
    c: Coincident(g133,g134)
    c: Coincident(g134,g131)
    c: Equal(g131,g132)
    c: Equal(g131,g133)
    c: Equal(g131,g134)
    c: PointOnObject(g131,g135)
    c: PointOnObject(g132,g135)
    c: PointOnObject(g133,g135)
    c: PointOnObject(g134,g135)
    c: Coincident(g135,g130)
    c: PointOnObject(g131,g130)
    c: Coincident(g136,g137)
    c: Coincident(g137,g138)
    c: Coincident(g138,g139)
    c: Coincident(g139,g136)
    c: Equal(g136,g137)
    c: Equal(g136,g138)
    c: Equal(g136,g139)
    c: PointOnObject(g136,g140)
    c: PointOnObject(g137,g140)
    c: PointOnObject(g138,g140)
    c: PointOnObject(g139,g140)
    c: Coincident(g140,g130)
    c: Parallel(g134,g139)
    c: Distance(g130,g136) = 7.5
    c: Coincident(g141,g142)
    c: Coincident(g142,g143)
    c: Coincident(g143,g144)
    c: Coincident(g144,g141)
    c: Equal(g141,g142)
    c: Equal(g141,g143)
    c: Equal(g141,g144)
    c: PointOnObject(g141,g145)
    c: PointOnObject(g142,g145)
    c: PointOnObject(g143,g145)
    c: PointOnObject(g144,g145)
    c: Coincident(g145,g130)
    c: Angle(g134,g141) = 0.785398
    c: Distance(g143,g130) = 5.5
    c: Coincident(g146,g131)
    c: PointOnObject(g146,g145)
    c: PointOnObject(g136,g146)
    c: Coincident(g147,g131)
    c: Coincident(g148,g133)
    c: Coincident(g149,g132)
    c: PointOnObject(g149,g145)
    c: PointOnObject(g149,g145)
    c: PointOnObject(g147,g145)
    c: PointOnObject(g148,g145)
    c: PointOnObject(g148,g145)
    c: PointOnObject(g137,g149)
    c: PointOnObject(g138,g148)
    c: PointOnObject(g136,g147)
    c: Coincident(g150,g146)
    c: Coincident(g149,g150)
    c: Coincident(g147,g152)
    c: Coincident(g152,g148)
    c: Coincident(g151,g148)
    c: Coincident(g151,g149)
    c: Equal(g129,g153) = 6.5
    c: Coincident(g153,g130)
    c: PointOnObject(g152,g153)
    c: PointOnObject(g151,g153)
    c: PointOnObject(g150,g153)
    c: Coincident(g130,g97)
    c: Coincident(g107,g99)
    c: Coincident(g154,g126)
    c: Coincident(g154,g125)
    c: PointOnObject(g154,g129)
    c: Coincident(g155,g97)
    c: Perpendicular(g136,g155)
    c: Coincident(g156,g99)
    c: Tangent(g105,g158) = 1.5708
    c: Tangent(g106,g159) = 1.5708
    c: Tangent(g157,g160) = 1.5708
    c: Radius(g158) = 3
    c: Radius(g160) = 3
    c: Radius(g159) = 3
    c: Tangent(g161,g165) = -1.5708
    c: Tangent(g123,g165) = 1.5708
    c: Tangent(g126,g166) = 1.5708
    c: Tangent(g162,g166) = 1.5708
    c: Tangent(g165,g129)
    c: Tangent(g166,g129)
    c: Tangent(g163,g167) = 1.5708
    c: Tangent(g147,g167) = 1.5708
    c: Tangent(g164,g168) = -1.5708
    c: Tangent(g146,g168) = 1.5708
    c: Tangent(g168,g153)
    c: Tangent(g167,g153)
    c: Distance(g164,g155) = 2
    c: Distance(g163,g155) = 2
    c: Diameter(g169) = 2.4  'M2-clear'
    c: Coincident(g169,g123)
    c: Equal(g169,g170) = 2.4  'M2-clear'
    c: Coincident(g170,g124)
    c: Equal(g169,g171) = 2.4  'M2-clear'
    c: Coincident(g171,g125)
    c: Equal(g169,g172) = 2.4  'M2-clear'
    c: Coincident(g172,g126)
    c: Distance(g162,g156) = 2
    c: Distance(g161,g156) = 2
    c: Equal(g169,g173) = 2.4  'M2-clear'
    c: Coincident(g173,g146)
    c: Equal(g169,g174) = 2.4  'M2-clear'
    c: Coincident(g174,g149)
    c: Equal(g169,g175) = 2.4  'M2-clear'
    c: Coincident(g175,g148)
    c: Equal(g169,g176) = 2.4  'M2-clear'
    c: Coincident(g176,g147)
    c: Coincident(g177,g99)
    c: Diameter(g177) = 5
    c: Equal(g177,g178) = 5
    c: Coincident(g178,g97)
    c: Vertical(g179)
    c: Coincident(g180,g159)
    c: Vertical(g180)
    c: PointOnObject(g156,g179)
    c: Coincident(g181,g158)
    c: Vertical(g181)
    c: Tangent(g181,g103)
    c: Vertical(g182)
    c: PointOnObject(g155,g182)
    c: Tangent(g104,g180)
    c: Tangent(g180,g159)
    c: Tangent(g158,g181)
    c: Tangent(g163,g183) = 1.5708
    c: Tangent(g181,g183) = -1.5708
    c: Tangent(g162,g184) = 1.5708
    c: Tangent(g180,g184) = -1.5708
    c: Coincident(g179,g180)
    c: Coincident(g181,g182)
    c: Radius(g183) = 4
    c: Radius(g184) = 5
    c: Perpendicular(g114,g156)
    c: PointOnObject(g185,g156)
    c: PointOnObject(g186,g156)
    c: Perpendicular(g156,g185)
    c: Perpendicular(g156,g186)
    c: Coincident(g186,g162)
    c: Distance(g185) = 3
    c: Distance(g186) = 3
    c: Perpendicular(g155,g188)
    c: Perpendicular(g155,g187)
    c: PointOnObject(g187,g155)
    c: PointOnObject(g188,g155)
    c: Coincident(g188,g163)
    c: Distance(g188) = 3
    c: Distance(g187) = 3
    c: Coincident(g106,g8)
    c: Coincident(g105,g9)
    c: Coincident(g98,g3)
    c: Coincident(g100,g1)
    c: DistanceY(g156,g58) = 0
    c: DistanceY(g155,g59) = 0
    c: Parallel(g73,g157)
    c: Coincident(g189,g60)
    c: Coincident(g190,g61)
    c: Coincident(g191,g62)
    c: Coincident(g192,g60)
    c: Radius(g189) = 1.2  'M2 Clear'
    c: Equal(g189,g192)
    c: Equal(g189,g190)
    c: Equal(g189,g191)
    c: Coincident(g194,g193)
    c: Vertical(g194)
    c: DistanceX(g-1,g193) = 17
    c: Tangent(g193,g194)
    c: Radius(g193) = 5
    c: Tangent(g194,g195) = 1.5708
    c: Tangent(g64,g195) = -1.5708
    c: Radius(g195) = 5
    c: DistanceX(g1,g90) = 12
    c: Vertical(g197)
    c: Vertical(g196)
    c: Tangent(g65,g198) = -1.5708
    c: Tangent(g197,g198) = -1.5708
    c: Tangent(g197,g199) = -1.5708
    c: Tangent(g69,g199) = -1.5708
    c: Tangent(g196,g200) = 1.5708
    c: Tangent(g164,g200) = -1.5708
    c: Radius(g200) = 5
    c: Equal(g200,g199)
    c: Equal(g200,g198)
    c: DistanceX(g196,g-1) = 17
    c: DistanceX(g-1,g197) = 17
    c: Vertical(g201)
    c: Tangent(g161,g202) = -1.5708
    c: Tangent(g201,g202) = 1.5708
    c: Tangent(g201,g203) = 1.5708
    c: Tangent(g157,g203) = -1.5708
    c: DistanceX(g180,g-1) = 12
    c: DistanceX(g201,g-1) = 17
    c: Radius(g203) = 5
    c: Equal(g203,g202)
    c: Coincident(g164,g187)
    c: Coincident(g69,g93)
    c: Coincident(g161,g185)
    c: PointOnObject(g182,g63)
    c: PointOnObject(g88,g63)
    c: PointOnObject(g179,g63)
    c: Coincident(g204,g160)
    c: Coincident(g205,g204)
    c: Coincident(g205,g196)
    c: Tangent(g205,g204)
    c: Tangent(g205,g196)
    c: Radius(g205) = 5
    c: Tangent(g204,g160)
    c: Distance(g204,g60) = 6
    c: Distance(g65,g61) = 6
    c: Distance(g64,g62) = 6
    c: Parallel(g204,g60)
    c: Distance(g157,g73) = 6
    c: Tangent(g193,g72) = -1.5708
    c: Diameter(g207) = 3
    c: Equal(g207,g206)
    c: Distance(g207,g106) = 4
    c: Distance(g206,g8) = 4
    c: Distance(g207,g206) = 18
    c: Distance(g206,g-2) = 9
FEATURE [PartDesign::Pad] Pad
  Direction = (1,1,1)
  Length = 5
  Length2 = 100
  Profile = -> Sketch
  Type = 0
FEATURE [Fem::FemSolverObjectPython] SolverCcxTools  # FEM object (typed FeaturePython)
  AnalysisType = 0
  BeamShellResultOutput3D = false
  EigenmodeHighLimit = 1000000
  EigenmodeLowLimit = 0
  EigenmodesCount = 10
  GeometricalNonlinearity = 0
  IterationsControlParameterCutb = 0.25,0.5,0.75,0.85,,,1.5,
  IterationsControlParameterIter = 4,8,9,200,10,400,,200,,
  IterationsControlParameterTimeUse = false
  IterationsThermoMechMaximum = 200
  IterationsUserDefinedIncrementations = false
  IterationsUserDefinedTimeStepLength = false
  MaterialNonlinearity = 0
  MatrixSolverType = 0
  SplitInputWriter = false
  ThermoMechSteadyState = true
  TimeEnd = 1
  TimeInitialStep = 1
FEATURE [Fem::FemMeshObjectPython] FEMMeshGmsh  # FEM object (typed FeaturePython)
  Algorithm2D = 0
  Algorithm3D = 0
  CharacteristicLengthMax = 3
  CharacteristicLengthMin = 0
  CoherenceMesh = true
  ElementDimension = 0
  ElementOrder = 1
  GeometryTolerance = 1e-06
  GroupsOfNodes = false
  HighOrderOptimize = false
  OptimizeNetgen = false
  OptimizeStd = true
  Part = -> Pad
  RecombineAll = false
  SecondOrderLinear = false
FEATURE [App::MaterialObjectPython] MaterialSolid  # material (typed FeaturePython)
  Category = 0
  Material = AuthorAndLicense=ABS-Generic,CardName=ABS-Generic,Density=1060 kg/m^3,+12 more (map truncated)
FEATURE [Fem::ConstraintFixed] ConstraintFixed
  NormalDirection = (0,-1,0)
  Normals = (18) [(0,-1,0),(0,-1,0),(0,-1,0),(0,-1,0),(0,-1,0),(0,-1,0),(0,-1,0),(0,-1,0),(0,-1,0),(0,-1,0),(0,-1,0),(0,-1,0),(0,-1,0),(0,-1,0),(0,-1,0),(0,-1,0),+2 more]
  Points = (18) [(0,-50,5),(-4.49999,-50,5),(-8.99997,-50,5),(0,-50,2.5),(-4.49999,-50,2.5),(-8.99997,-50,2.5),(0,-50,0),(-4.49999,-50,0),(-8.99997,-50,0),(9,-50,5),+8 more]
  References = -> [Pad]
FEATURE [Fem::ConstraintForce] ConstraintForce
  DirectionVector = (-0.309261,-0.950977,0)
  Force = 20
  NormalDirection = (0.309261,0.950977,0)
  Points = (9) [(57.027,44.2079,5),(55.0695,47.8823,5),(51.3251,46.0622,5),(57.027,44.2079,2.5),(55.0695,47.8823,2.5),(51.3251,46.0622,2.5),(57.027,44.2079,0),+2 more]
  References = -> [Pad]
  Reversed = true
FEATURE [Fem::FemAnalysis] Analysis
  Group = -> [SolverCcxTools,FEMMeshGmsh,MaterialSolid,ConstraintFixed,ConstraintForce]
FEATURE [Sketcher::SketchObject] Sketch001  label="HappymodelELRS24"
  FullyConstrained = true
  MapMode = 5
  Support = -> [XY_Plane]
  sketch-geometry (109):
    g0: LineSegment StartX=17.6777 StartY=0 StartZ=0 EndX=0 EndY=17.6777 EndZ=0
    g1: LineSegment StartX=0 StartY=17.6777 StartZ=0 EndX=-17.6777 EndY=-3.6e-15 EndZ=0
    g2: LineSegment StartX=-17.6777 StartY=-3.6e-15 StartZ=0 EndX=0 EndY=-17.6777 EndZ=0
    g3: LineSegment StartX=0 StartY=-17.6777 StartZ=0 EndX=17.6777 EndY=0 EndZ=0
    g4: Circle CenterX=0 CenterY=0 CenterZ=0 NormalX=0 NormalY=0 NormalZ=1 AngleXU=0 Radius=17.6777
    g5: LineSegment StartX=-3.625 StartY=-12.6777 StartZ=0 EndX=3.625 EndY=-12.6777 EndZ=0
    g6: LineSegment StartX=3.625 StartY=-12.6777 StartZ=0 EndX=3.625 EndY=-13.9277 EndZ=0
    g7: LineSegment StartX=2.625 StartY=-14.9277 StartZ=0 EndX=-2.625 EndY=-14.9277 EndZ=0
    g8: LineSegment StartX=-3.625 StartY=-13.9277 StartZ=0 EndX=-3.625 EndY=-12.6777 EndZ=0
    g9: LineSegment StartX=-3.625 StartY=-13.9277 StartZ=0 EndX=-2.625 EndY=-14.9277 EndZ=0
    g10: LineSegment StartX=2.625 StartY=-14.9277 StartZ=0 EndX=3.625 EndY=-13.9277 EndZ=0
    g11: LineSegment StartX=11.3073 StartY=-7.63038 StartZ=0 EndX=15.1964 EndY=-3.7413 EndZ=0
    g12: LineSegment StartX=15.1964 StartY=-3.7413 StartZ=0 EndX=12.9337 EndY=-1.47855 EndZ=0
    g13: LineSegment StartX=12.9337 StartY=-1.47855 StartZ=0 EndX=9.0446 EndY=-5.36764 EndZ=0
    g14: LineSegment StartX=9.0446 StartY=-5.36764 StartZ=0 EndX=11.3073 EndY=-7.63038 EndZ=0
    g15: LineSegment StartX=-12.9337 StartY=1.47855 StartZ=0 EndX=-9.0446 EndY=5.36764 EndZ=0
    g16: LineSegment StartX=-9.0446 StartY=5.36764 StartZ=0 EndX=-11.3073 EndY=7.63038 EndZ=0
    g17: LineSegment StartX=-11.3073 StartY=7.63038 StartZ=0 EndX=-15.1964 EndY=3.7413 EndZ=0
    g18: LineSegment StartX=-15.1964 StartY=3.7413 StartZ=0 EndX=-12.9337 EndY=1.47855 EndZ=0
    g19: LineSegment StartX=-15.2589 StartY=-3.8038 StartZ=0 EndX=-11.3698 EndY=-7.69288 EndZ=0
    g20: LineSegment StartX=-11.3698 StartY=-7.69288 StartZ=0 EndX=-9.1071 EndY=-5.43014 EndZ=0
    g21: LineSegment StartX=-9.1071 StartY=-5.43014 StartZ=0 EndX=-12.9962 EndY=-1.54105 EndZ=0
    g22: LineSegment StartX=-12.9962 StartY=-1.54105 StartZ=0 EndX=-15.2589 EndY=-3.8038 EndZ=0
    g23: Circle CenterX=0 CenterY=-17.6777 CenterZ=0 NormalX=0 NormalY=0 NormalZ=1 AngleXU=0 Radius=1.5
    g24: ArcOfCircle CenterX=0 CenterY=-17.6777 CenterZ=0 NormalX=0 NormalY=0 NormalZ=1 AngleXU=0 Radius=1.5 StartAngle=4.68035e-08 EndAngle=3.14159
    g25: LineSegment StartX=1.5 StartY=-17.6777 StartZ=0 EndX=1.5 EndY=-18.5527 EndZ=0
    g26: LineSegment StartX=-1.5 StartY=-17.6777 StartZ=0 EndX=-1.5 EndY=-18.5527 EndZ=0
    g27: LineSegment StartX=-1.5 StartY=-18.5527 StartZ=0 EndX=1.5 EndY=-18.5527 EndZ=0
    g28: LineSegment StartX=-1.5 StartY=-18.5527 StartZ=0 EndX=-3.62132 EndY=-16.4313 EndZ=0
    g29: LineSegment StartX=1.5 StartY=-18.5527 StartZ=0 EndX=3.62132 EndY=-16.4313 EndZ=0
    g30: LineSegment StartX=-3.62132 StartY=-16.4313 StartZ=0 EndX=-3.12635 EndY=-15.9364 EndZ=0
    g31: LineSegment StartX=3.62132 StartY=-16.4313 StartZ=0 EndX=3.06385 EndY=-15.8739 EndZ=0
    g32: Circle CenterX=17.6777 CenterY=0 CenterZ=0 NormalX=0 NormalY=0 NormalZ=1 AngleXU=0 Radius=1.5
    g33: ArcOfCircle CenterX=17.6777 CenterY=0 CenterZ=0 NormalX=0 NormalY=0 NormalZ=1 AngleXU=0 Radius=1.5 StartAngle=1.5708 EndAngle=4.71239
    g34: LineSegment StartX=17.6777 StartY=1.5 StartZ=0 EndX=18.4277 EndY=1.5 EndZ=0
    g35: LineSegment StartX=17.6777 StartY=-1.5 StartZ=0 EndX=18.4277 EndY=-1.5 EndZ=0
    g36: LineSegment StartX=18.4277 StartY=-1.5 StartZ=0 EndX=18.4277 EndY=1.5 EndZ=0
    g37: LineSegment StartX=18.4277 StartY=-1.5 StartZ=0 EndX=16.3063 EndY=-3.62132 EndZ=0
    g38: LineSegment StartX=18.4277 StartY=1.5 StartZ=0 EndX=16.3063 EndY=3.62132 EndZ=0
    g39: LineSegment StartX=16.3063 StartY=-3.62132 StartZ=0 EndX=15.8114 EndY=-3.12635 EndZ=0
    g40: LineSegment StartX=16.3063 StartY=3.62132 StartZ=0 EndX=15.8114 EndY=3.12635 EndZ=0
    g41: Circle CenterX=-17.6777 CenterY=-3.6e-15 CenterZ=0 NormalX=0 NormalY=0 NormalZ=1 AngleXU=0 Radius=1.5
    g42: ArcOfCircle CenterX=-17.6777 CenterY=-3.6e-15 CenterZ=0 NormalX=0 NormalY=0 NormalZ=1 AngleXU=0 Radius=1.5 StartAngle=4.71239 EndAngle=7.85398
    g43: LineSegment StartX=-17.6777 StartY=-1.5 StartZ=0 EndX=-18.4277 EndY=-1.5 EndZ=0
    g44: LineSegment StartX=-17.6777 StartY=1.5 StartZ=0 EndX=-18.4277 EndY=1.5 EndZ=0
    g45: LineSegment StartX=-18.4277 StartY=1.5 StartZ=0 EndX=-18.4277 EndY=-1.5 EndZ=0
    g46: LineSegment StartX=-18.4277 StartY=1.5 StartZ=0 EndX=-16.3063 EndY=3.62132 EndZ=0
    g47: LineSegment StartX=-18.4277 StartY=-1.5 StartZ=0 EndX=-16.3063 EndY=-3.62132 EndZ=0
    g48: LineSegment StartX=-16.3063 StartY=3.62132 StartZ=0 EndX=-15.8114 EndY=3.12635 EndZ=0
    g49: Circle CenterX=0 CenterY=17.6777 CenterZ=0 NormalX=0 NormalY=0 NormalZ=1 AngleXU=0 Radius=1.5
    g50: ArcOfCircle CenterX=0 CenterY=17.6777 CenterZ=0 NormalX=0 NormalY=0 NormalZ=1 AngleXU=0 Radius=1.5 StartAngle=3.14159 EndAngle=6.28319
    g51: LineSegment StartX=-1.5 StartY=17.6777 StartZ=0 EndX=-1.5 EndY=18.4277 EndZ=0
    g52: LineSegment StartX=1.5 StartY=17.6777 StartZ=0 EndX=1.5 EndY=18.4277 EndZ=0
    g53: LineSegment StartX=1.5 StartY=18.4277 StartZ=0 EndX=-1.5 EndY=18.4277 EndZ=0
    g54: LineSegment StartX=1.5 StartY=18.4277 StartZ=0 EndX=3.62132 EndY=16.3063 EndZ=0
    g55: LineSegment StartX=-1.5 StartY=18.4277 StartZ=0 EndX=-3.62132 EndY=16.3063 EndZ=0
    g56: LineSegment StartX=3.62132 StartY=16.3063 StartZ=0 EndX=3.12635 EndY=15.8114 EndZ=0
    g57: LineSegment StartX=-3.62132 StartY=16.3063 StartZ=0 EndX=-3.12635 EndY=15.8114 EndZ=0
    g58: LineSegment StartX=3.12635 StartY=15.8114 StartZ=0 EndX=15.8114 EndY=3.12635 EndZ=0
    g59: LineSegment StartX=-3.12635 StartY=15.8114 StartZ=0 EndX=-15.8114 EndY=3.12635 EndZ=0
    g60: LineSegment StartX=-3.12635 StartY=-15.9364 StartZ=0 EndX=-15.8739 EndY=-3.18885 EndZ=0
    g61: LineSegment StartX=3.06385 StartY=-15.8739 StartZ=0 EndX=15.8114 EndY=-3.12635 EndZ=0
    g62: Circle CenterX=-5.56477 CenterY=-12.6494 CenterZ=0 NormalX=0 NormalY=0 NormalZ=1 AngleXU=0 Radius=0.5
    g63: Circle CenterX=-6.97899 CenterY=-11.2352 CenterZ=0 NormalX=0 NormalY=0 NormalZ=1 AngleXU=0 Radius=0.5
    g64: LineSegment StartX=13.6408 StartY=-1.47855 StartZ=0 EndX=15.1964 EndY=-3.03419 EndZ=0
    g65: LineSegment StartX=15.1964 StartY=-4.4484 StartZ=0 EndX=12.0144 EndY=-7.63038 EndZ=0
    g66: LineSegment StartX=10.6002 StartY=-7.63038 StartZ=0 EndX=9.0446 EndY=-6.07475 EndZ=0
    g67: LineSegment StartX=9.0446 StartY=-4.66053 StartZ=0 EndX=12.2266 EndY=-1.47855 EndZ=0
    g68: ArcOfCircle CenterX=12.9337 CenterY=-2.18566 CenterZ=0 NormalX=0 NormalY=0 NormalZ=1 AngleXU=0 Radius=1 StartAngle=0.785398 EndAngle=2.35619
    g69: ArcOfCircle CenterX=14.4893 CenterY=-3.7413 CenterZ=0 NormalX=0 NormalY=0 NormalZ=1 AngleXU=0 Radius=1 StartAngle=5.49779 EndAngle=7.06858
    g70: ArcOfCircle CenterX=11.3073 CenterY=-6.92328 CenterZ=0 NormalX=0 NormalY=0 NormalZ=1 AngleXU=0 Radius=1 StartAngle=3.92699 EndAngle=5.49779
    g71: ArcOfCircle CenterX=9.7517 CenterY=-5.36764 CenterZ=0 NormalX=0 NormalY=0 NormalZ=1 AngleXU=0 Radius=1 StartAngle=2.35619 EndAngle=3.92699
    g72: LineSegment StartX=15.1964 StartY=3.7413 StartZ=0 EndX=11.3073 EndY=7.63038 EndZ=0
    g73: LineSegment StartX=11.3073 StartY=7.63038 StartZ=0 EndX=9.0446 EndY=5.36764 EndZ=0
    g74: LineSegment StartX=9.0446 StartY=5.36764 StartZ=0 EndX=12.9337 EndY=1.47855 EndZ=0
    g75: LineSegment StartX=12.9337 StartY=1.47855 StartZ=0 EndX=15.1964 EndY=3.7413 EndZ=0
    g76: LineSegment StartX=9.0446 StartY=6.07475 StartZ=0 EndX=10.6002 EndY=7.63038 EndZ=0
    g77: LineSegment StartX=12.0144 StartY=7.63038 StartZ=0 EndX=15.9035 EndY=3.7413 EndZ=0
    g78: LineSegment StartX=15.9035 StartY=2.32708 StartZ=0 EndX=14.3479 EndY=0.771447 EndZ=0
    g79: LineSegment StartX=12.9337 StartY=0.771447 StartZ=0 EndX=9.0446 EndY=4.66053 EndZ=0
    g80: ArcOfCircle CenterX=9.7517 CenterY=5.36764 CenterZ=0 NormalX=0 NormalY=0 NormalZ=1 AngleXU=0 Radius=1 StartAngle=2.35619 EndAngle=3.92699
    g81: ArcOfCircle CenterX=11.3073 CenterY=6.92328 CenterZ=0 NormalX=0 NormalY=0 NormalZ=1 AngleXU=0 Radius=1 StartAngle=0.785398 EndAngle=2.35619
    g82: ArcOfCircle CenterX=15.1964 CenterY=3.03419 CenterZ=0 NormalX=0 NormalY=0 NormalZ=1 AngleXU=0 Radius=1 StartAngle=5.49779 EndAngle=7.06858
    g83: ArcOfCircle CenterX=13.6408 CenterY=1.47855 CenterZ=0 NormalX=0 NormalY=0 NormalZ=1 AngleXU=0 Radius=1 StartAngle=3.92699 EndAngle=5.49779
    g84: LineSegment StartX=-16.3063 StartY=-3.62132 StartZ=0 EndX=-15.8739 EndY=-3.18885 EndZ=0
    g85: LineSegment StartX=-12.2891 StartY=-1.54105 StartZ=0 EndX=-9.1071 EndY=-4.72303 EndZ=0
    g86: LineSegment StartX=-9.1071 StartY=-6.13725 StartZ=0 EndX=-10.6627 EndY=-7.69288 EndZ=0
    g87: LineSegment StartX=-12.0769 StartY=-7.69288 StartZ=0 EndX=-15.2589 EndY=-4.5109 EndZ=0
    g88: LineSegment StartX=-15.2589 StartY=-3.09669 StartZ=0 EndX=-13.7033 EndY=-1.54105 EndZ=0
    g89: ArcOfCircle CenterX=-9.8142 CenterY=-5.43014 CenterZ=0 NormalX=0 NormalY=0 NormalZ=1 AngleXU=0 Radius=1 StartAngle=5.49779 EndAngle=7.06858
    g90: ArcOfCircle CenterX=-11.3698 CenterY=-6.98578 CenterZ=0 NormalX=0 NormalY=0 NormalZ=1 AngleXU=0 Radius=1 StartAngle=3.92699 EndAngle=5.49779
    g91: ArcOfCircle CenterX=-14.5518 CenterY=-3.8038 CenterZ=0 NormalX=0 NormalY=0 NormalZ=1 AngleXU=0 Radius=1 StartAngle=2.35619 EndAngle=3.92699
    g92: ArcOfCircle CenterX=-12.9962 CenterY=-2.24816 CenterZ=0 NormalX=0 NormalY=0 NormalZ=1 AngleXU=0 Radius=1 StartAngle=0.785398 EndAngle=2.35619
    g93: LineSegment StartX=-14.3479 StartY=0.771447 StartZ=0 EndX=-15.9035 EndY=2.32708 EndZ=0
    g94: LineSegment StartX=-15.9035 StartY=3.7413 StartZ=0 EndX=-7.41825 EndY=12.2266 EndZ=0
    g95: LineSegment StartX=-6.00404 StartY=12.2266 StartZ=0 EndX=-4.4484 EndY=10.6709 EndZ=0
    g96: LineSegment StartX=-4.4484 StartY=9.25673 StartZ=0 EndX=-12.9337 EndY=0.771447 EndZ=0
    g97: ArcOfCircle CenterX=-15.1964 CenterY=3.03419 CenterZ=0 NormalX=0 NormalY=0 NormalZ=1 AngleXU=0 Radius=1 StartAngle=2.35619 EndAngle=3.92699
    g98: ArcOfCircle CenterX=-6.71114 CenterY=11.5195 CenterZ=0 NormalX=0 NormalY=0 NormalZ=1 AngleXU=0 Radius=1 StartAngle=0.785398 EndAngle=2.35619
    g99: ArcOfCircle CenterX=-5.15551 CenterY=9.96383 CenterZ=0 NormalX=0 NormalY=0 NormalZ=1 AngleXU=0 Radius=1 StartAngle=5.49779 EndAngle=7.06858
    g100: ArcOfCircle CenterX=-13.6408 CenterY=1.47855 CenterZ=0 NormalX=0 NormalY=0 NormalZ=1 AngleXU=0 Radius=1 StartAngle=3.92699 EndAngle=5.49779
    g101: LineSegment StartX=-3.125 StartY=-12.1777 StartZ=0 EndX=3.125 EndY=-12.1777 EndZ=0
    g102: LineSegment StartX=4.125 StartY=-13.1777 StartZ=0 EndX=4.125 EndY=-14.4277 EndZ=0
    g103: ArcOfCircle CenterX=3.125 CenterY=-13.1777 CenterZ=0 NormalX=0 NormalY=0 NormalZ=1 AngleXU=0 Radius=1 StartAngle=0 EndAngle=1.5708
    g104: ArcOfCircle CenterX=3.125 CenterY=-14.4277 CenterZ=0 NormalX=0 NormalY=0 NormalZ=1 AngleXU=0 Radius=1 StartAngle=4.71239 EndAngle=6.28319
    g105: ArcOfCircle CenterX=-3.125 CenterY=-14.4277 CenterZ=0 NormalX=0 NormalY=0 NormalZ=1 AngleXU=0 Radius=1 StartAngle=3.14159 EndAngle=4.71239
    g106: LineSegment StartX=-4.125 StartY=-14.4277 StartZ=0 EndX=-4.125 EndY=-13.1777 EndZ=0
    g107: ArcOfCircle CenterX=-3.125 CenterY=-13.1777 CenterZ=0 NormalX=0 NormalY=0 NormalZ=1 AngleXU=0 Radius=1 StartAngle=1.5708 EndAngle=3.14159
    g108: LineSegment StartX=3.125 StartY=-15.4277 StartZ=0 EndX=-3.125 EndY=-15.4277 EndZ=0
  constraints (294):
    c: Coincident(g0,g1)
    c: Coincident(g1,g2)
    c: Coincident(g2,g3)
    c: Coincident(g3,g0)
    c: Equal(g0,g1)
    c: Equal(g0,g2)
    c: Equal(g0,g3)
    c: PointOnObject(g0,g4)
    c: PointOnObject(g1,g4)
    c: PointOnObject(g2,g4)
    c: PointOnObject(g3,g4)
    c: Coincident(g4,g-1)
    c: PointOnObject(g0,g-2)
    c: Horizontal(g5)
    c: Coincident(g5,g6)
    c: Horizontal(g7)
    c: Coincident(g8,g5)
    c: Distance(g2,g5) = 5
    c: Distance(g5) = 7.25
    c: Vertical(g8)
    c: Vertical(g6)
    c: Coincident(g9,g8)
    c: Coincident(g9,g7)
    c: Coincident(g10,g7)
    c: Coincident(g10,g6)
    c: Parallel(g9,g2)
    c: Parallel(g10,g3)
    c: Equal(g8,g6)
    c: Distance(g5,g-2) = 3.625
    c: Coincident(g11,g12)
    c: Coincident(g12,g13)
    c: Coincident(g13,g14)
    c: Coincident(g14,g11)
    c: Distance(g11) = 5.5
    c: Distance(g12) = 3.2
    c: Equal(g13,g11)
    c: Equal(g14,g12)
    c: Perpendicular(g11,g14)
    c: Coincident(g15,g16)
    c: Coincident(g16,g17)
    c: Coincident(g17,g18)
    c: Coincident(g18,g15)
    c: Equal(g11,g15) = 4.8
    c: Equal(g12,g16) = 2.7
    c: Equal(g17,g15)
    c: Equal(g18,g16)
    c: Perpendicular(g15,g18)
    c: Coincident(g19,g20)
    c: Coincident(g20,g21)
    c: Coincident(g21,g22)
    c: Coincident(g22,g19)
    c: Equal(g11,g19) = 4.8
    c: Equal(g12,g20) = 2.7
    c: Equal(g21,g19)
    c: Equal(g22,g20)
    c: Perpendicular(g19,g22)
    c: Parallel(g11,g3)
    c: Parallel(g17,g1)
    c: Parallel(g19,g2)
    c: Distance(g2,g14) = 15.1
    c: Distance(g2,g20) = 15.1
    c: Distance(g0,g16) = 15.1
    c: Coincident(g23,g2)
    c: Coincident(g24,g2)
    c: Diameter(g23) = 3
    c: Equal(g24,g23)
    c: Coincident(g25,g24)
    c: Coincident(g26,g24)
    c: Parallel(g26,g25)
    c: Equal(g26,g25)
    c: Tangent(g26,g24)
    c: Coincident(g27,g26)
    c: Coincident(g27,g25)
    c: Perpendicular(g26,g27)
    c: Distance(g24,g27) = 0.875
    c: Coincident(g28,g26)
    c: Coincident(g29,g25)
    c: Coincident(g30,g28)
    c: Coincident(g31,g29)
    c: Perpendicular(g28,g30)
    c: Perpendicular(g29,g31)
    c: Angle(g26,g28) = 0.785398
    c: Angle(g29,g25) = 0.785398
    c: Equal(g29,g28)
    c: Distance(g28) = 3
    c: Equal(g23,g32) = 2.75
    c: Equal(g33,g32)
    c: Coincident(g34,g33)
    c: Coincident(g35,g33)
    c: Parallel(g35,g34)
    c: Equal(g35,g34)
    c: Tangent(g35,g33)
    c: Coincident(g36,g35)
    c: Coincident(g36,g34)
    c: Perpendicular(g35,g36)
    c: Distance(g33,g36) = 0.75
    c: Coincident(g37,g35)
    c: Coincident(g38,g34)
    c: Coincident(g39,g37)
    c: Coincident(g40,g38)
    c: Perpendicular(g37,g39)
    c: Perpendicular(g38,g40)
    c: Angle(g35,g37) = 0.785398
    c: Angle(g38,g34) = 0.785398
    c: Equal(g38,g37)
    c: Equal(g28,g37) = 2.5
    c: Coincident(g32,g33)
    c: Coincident(g0,g33)
    c: Parallel(g37,g3)
    c: Equal(g23,g41) = 2.75
    c: Equal(g42,g41)
    c: Coincident(g43,g42)
    c: Coincident(g44,g42)
    c: Parallel(g44,g43)
    c: Equal(g44,g43)
    c: Tangent(g44,g42)
    c: Coincident(g45,g44)
    c: Coincident(g45,g43)
    c: Perpendicular(g44,g45)
    c: Distance(g42,g45) = 0.75
    c: Coincident(g46,g44)
    c: Coincident(g47,g43)
    c: Coincident(g48,g46)
    c: Perpendicular(g46,g48)
    c: Angle(g44,g46) = 0.785398
    c: Angle(g47,g43) = 0.785398
    c: Equal(g47,g46)
    c: Equal(g28,g46) = 2.5
    c: Coincident(g42,g1)
    c: Coincident(g41,g42)
    c: Equal(g23,g49) = 2.75
    c: Equal(g50,g49)
    c: Coincident(g51,g50)
    c: Coincident(g52,g50)
    c: Parallel(g52,g51)
    c: Equal(g52,g51)
    c: Tangent(g52,g50)
    c: Coincident(g53,g52)
    c: Coincident(g53,g51)
    c: Perpendicular(g52,g53)
    c: Distance(g50,g53) = 0.75
    c: Coincident(g54,g52)
    c: Coincident(g55,g51)
    c: Coincident(g56,g54)
    c: Coincident(g57,g55)
    c: Perpendicular(g54,g56)
    c: Perpendicular(g55,g57)
    c: Angle(g52,g54) = 0.785398
    c: Angle(g55,g51) = 0.785398
    c: Equal(g55,g54)
    c: Equal(g28,g54) = 2.5
    c: Coincident(g50,g0)
    c: Parallel(g54,g0)
    c: Coincident(g58,g56)
    c: Coincident(g58,g40)
    c: Coincident(g59,g57)
    c: Coincident(g60,g30)
    c: Coincident(g61,g31)
    c: Coincident(g61,g39)
    c: Coincident(g59,g48)
    c: Parallel(g46,g1)
    c: Coincident(g49,g50)
    c: Tangent(g19,g60)
    c: Tangent(g11,g61)
    c: Tangent(g59,g17)
    c: DistanceY(g8,g8) = 1.25
    c: Distance(g62,g24) = 7.5
    c: Diameter(g62) = 1
    c: Diameter(g63) = 1
    c: Tangent(g67,g68) = 1.5708
    c: Tangent(g64,g68) = 1.5708
    c: Tangent(g64,g69) = 1.5708
    c: Tangent(g65,g69) = 1.5708
    c: Tangent(g65,g70) = 1.5708
    c: Tangent(g66,g70) = 1.5708
    c: Tangent(g66,g71) = 1.5708
    c: Tangent(g67,g71) = 1.5708
    c: Parallel(g67,g13)
    c: Parallel(g65,g67)
    c: Parallel(g64,g12)
    c: Parallel(g66,g14)
    c: Radius(g71) = 1
    c: Equal(g71,g68)
    c: Equal(g71,g69)
    c: Equal(g71,g70)
    c: Distance(g65,g61) = 0.5
    c: Distance(g66,g14) = 0.5
    c: Distance(g67,g13) = 0.5
    c: Distance(g64,g12) = 0.5
    c: Coincident(g72,g73)
    c: Coincident(g73,g74)
    c: Coincident(g74,g75)
    c: Coincident(g75,g72)
    c: Equal(g11,g72) = 5.83
    c: Equal(g12,g73) = 3.2
    c: Equal(g74,g72)
    c: Equal(g75,g73)
    c: Perpendicular(g72,g75)
    c: Tangent(g79,g80) = 1.5708
    c: Tangent(g76,g80) = 1.5708
    c: Tangent(g76,g81) = 1.5708
    c: Tangent(g77,g81) = 1.5708
    c: Tangent(g77,g82) = 1.5708
    c: Tangent(g78,g82) = 1.5708
    c: Tangent(g78,g83) = 1.5708
    c: Tangent(g79,g83) = 1.5708
    c: Parallel(g79,g74)
    c: Parallel(g77,g79)
    c: Parallel(g76,g73)
    c: Parallel(g78,g75)
    c: Equal(g71,g83) = 1
    c: Equal(g83,g80)
    c: Equal(g83,g81)
    c: Equal(g83,g82)
    c: Distance(g78,g75) = 1.5
    c: Distance(g79,g74) = 0.5
    c: Distance(g76,g73) = 0.5
    c: Distance(g39) = 0.7
    c: Distance(g77,g72) = 0.5
    c: Tangent(g72,g58)
    c: Distance(g50,g73) = 15.1
    c: Coincident(g84,g47)
    c: Coincident(g84,g60)
    c: Parallel(g28,g2)
    c: Perpendicular(g47,g84)
    c: Equal(g39,g30)
    c: Equal(g30,g48)
    c: Equal(g48,g56)
    c: Equal(g39,g40)
    c: Distance(g24,g33) = 25
    c: Distance(g7,g5) = 2.25
    c: Tangent(g85,g89) = 1.5708
    c: Tangent(g86,g89) = 1.5708
    c: Tangent(g86,g90) = 1.5708
    c: Tangent(g87,g90) = 1.5708
    c: Tangent(g87,g91) = 1.5708
    c: Tangent(g88,g91) = 1.5708
    c: Tangent(g88,g92) = 1.5708
    c: Tangent(g85,g92) = 1.5708
    c: Radius(g92) = 1
    c: Equal(g92,g89)
    c: Equal(g92,g90)
    c: Equal(g92,g91)
    c: Parallel(g85,g87)
    c: Parallel(g88,g86)
    c: Perpendicular(g85,g86)
    c: Parallel(g85,g21)
    c: Tangent(g93,g97) = 1.5708
    c: Tangent(g94,g97) = 1.5708
    c: Tangent(g94,g98) = 1.5708
    c: Tangent(g95,g98) = 1.5708
    c: Tangent(g95,g99) = 1.5708
    c: Tangent(g96,g99) = 1.5708
    c: Tangent(g96,g100) = 1.5708
    c: Tangent(g93,g100) = 1.5708
    c: Radius(g100) = 1
    c: Equal(g100,g97)
    c: Equal(g100,g98)
    c: Equal(g100,g99)
    c: Parallel(g93,g95)
    c: Parallel(g96,g94)
    c: Perpendicular(g93,g94)
    c: Distance(g96,g15) = 0.5
    c: Distance(g94,g17) = 0.5
    c: Parallel(g15,g96)
    c: Distance(g93,g18) = 1.5
    c: Distance(g95,g16) = 7
    c: Distance(g85,g21) = 0.5
    c: Distance(g88,g22) = 0.5
    c: Distance(g87,g19) = 0.5
    c: Distance(g86,g20) = 0.5
    c: Distance(g62,g60) = 0.6
    c: Distance(g63,g60) = 0.6
    c: Distance(g63,g62) = 2
    c: Tangent(g101,g103) = 1.5708
    c: Tangent(g102,g103) = 1.5708
    c: Tangent(g102,g104) = 1.5708
    c: Tangent(g108,g104) = 1.5708
    c: Tangent(g108,g105) = 1.5708
    c: Tangent(g106,g105) = 1.5708
    c: Tangent(g106,g107) = 1.5708
    c: Tangent(g101,g107) = 1.5708
    c: Equal(g92,g107) = 1
    c: Equal(g107,g103)
    c: Equal(g107,g104)
    c: Equal(g107,g105)
    c: Parallel(g101,g108)
    c: Parallel(g106,g102)
    c: Perpendicular(g101,g102)
    c: Parallel(g101,g5)
    c: Distance(g101,g5) = 0.5
    c: Distance(g102,g6) = 0.5
    c: Distance(g106,g8) = 0.5
    c: Distance(g7,g108) = 0.5
FEATURE [Spreadsheet::Sheet] Spreadsheet
  cells = A1=Prop Diameter; B1(PropDiameter)=76.5; A2=Prop Clearance; B2(PropClearance)=3; A4=Motor wire; B4(Wire_clearance_distance)=44
FEATURE [Sketcher::SketchObject] Sketch002  label="Clearance"
  FullyConstrained = true
  MapMode = 5
  Support = -> [XY_Plane]
  sketch-geometry (33):
    g0: ArcOfCircle CenterX=17.6777 CenterY=0 CenterZ=0 NormalX=0 NormalY=0 NormalZ=1 AngleXU=0 Radius=2.2 StartAngle=2.08617 EndAngle=4.19702
    g1: ArcOfCircle CenterX=-17.6777 CenterY=0 CenterZ=0 NormalX=0 NormalY=0 NormalZ=1 AngleXU=0 Radius=2.2 StartAngle=5.22776 EndAngle=7.33861
    g2: LineSegment StartX=-16.9148 StartY=4.28007 StartZ=0 EndX=-10.5 EndY=10.6948 EndZ=0
    g3: LineSegment StartX=10.5 StartY=10.6948 StartZ=0 EndX=16.9148 EndY=4.28007 EndZ=0
    g4: LineSegment StartX=16.9148 StartY=-4.28007 StartZ=0 EndX=10.5 EndY=-10.6948 EndZ=0
    g5: LineSegment StartX=-10.5 StartY=-10.6948 StartZ=0 EndX=-16.9148 EndY=-4.28007 EndZ=0
    g6: LineSegment StartX=17.6777 StartY=0 StartZ=0 EndX=0 EndY=17.6777 EndZ=0
    g7: LineSegment StartX=0 StartY=17.6777 StartZ=0 EndX=-17.6777 EndY=0 EndZ=0
    g8: LineSegment StartX=-17.6777 StartY=0 StartZ=0 EndX=0 EndY=-17.6777 EndZ=0
    g9: LineSegment StartX=0 StartY=-17.6777 StartZ=0 EndX=17.6777 EndY=0 EndZ=0
    g10: Circle CenterX=0 CenterY=0 CenterZ=0 NormalX=0 NormalY=0 NormalZ=1 AngleXU=0 Radius=17.6777
    g11: ArcOfCircle CenterX=15.8541 CenterY=3.21941 CenterZ=0 NormalX=0 NormalY=0 NormalZ=1 AngleXU=0 Radius=1.5 StartAngle=5.22776 EndAngle=7.06858
    g12: ArcOfCircle CenterX=15.8541 CenterY=-3.21941 CenterZ=0 NormalX=0 NormalY=0 NormalZ=1 AngleXU=0 Radius=1.5 StartAngle=5.49779 EndAngle=7.33861
    g13: ArcOfCircle CenterX=-15.8541 CenterY=-3.21941 CenterZ=0 NormalX=0 NormalY=0 NormalZ=1 AngleXU=0 Radius=1.5 StartAngle=2.08617 EndAngle=3.92699
    g14: ArcOfCircle CenterX=-15.8541 CenterY=3.21941 CenterZ=0 NormalX=0 NormalY=0 NormalZ=1 AngleXU=0 Radius=1.5 StartAngle=2.35619 EndAngle=4.19702
    g15: LineSegment StartX=0 StartY=17.6777 StartZ=0 EndX=0 EndY=-17.6777 EndZ=0
    g16: LineSegment StartX=-10.25 StartY=38.5 StartZ=0 EndX=10.25 EndY=38.5 EndZ=0
    g17: LineSegment StartX=10.5 StartY=38.25 StartZ=0 EndX=10.5 EndY=-38.25 EndZ=0
    g18: LineSegment StartX=10.25 StartY=-38.5 StartZ=0 EndX=-10.25 EndY=-38.5 EndZ=0
    g19: LineSegment StartX=-10.5 StartY=-38.25 StartZ=0 EndX=-10.5 EndY=38.25 EndZ=0
    g20: ArcOfCircle CenterX=-10.25 CenterY=-38.25 CenterZ=0 NormalX=0 NormalY=0 NormalZ=1 AngleXU=0 Radius=0.25 StartAngle=3.14159 EndAngle=4.71239
    g21: ArcOfCircle CenterX=10.25 CenterY=-38.25 CenterZ=0 NormalX=0 NormalY=0 NormalZ=1 AngleXU=0 Radius=0.25 StartAngle=4.71239 EndAngle=6.28319
    g22: ArcOfCircle CenterX=10.25 CenterY=38.25 CenterZ=0 NormalX=0 NormalY=0 NormalZ=1 AngleXU=0 Radius=0.25 StartAngle=1.03e-14 EndAngle=1.5708
    g23: LineSegment StartX=-13.8724 StartY=8.73668 StartZ=0 EndX=-14.2215 EndY=9.08579 EndZ=0
    g24: LineSegment StartX=-14.2215 StartY=10.5 StartZ=0 EndX=-10.5 EndY=14.2215 EndZ=0
    g25: ArcOfCircle CenterX=-13.5144 CenterY=9.79289 CenterZ=0 NormalX=0 NormalY=0 NormalZ=1 AngleXU=0 Radius=1 StartAngle=2.35619 EndAngle=3.92699
    g26: LineSegment StartX=-13.8724 StartY=7.32247 StartZ=0 EndX=-16.9148 EndY=4.28007 EndZ=0
    g27: ArcOfCircle CenterX=-14.5795 CenterY=8.02957 CenterZ=0 NormalX=0 NormalY=0 NormalZ=1 AngleXU=0 Radius=1 StartAngle=5.49779 EndAngle=7.06858
    g28: LineSegment StartX=10.5 StartY=10.6948 StartZ=0 EndX=10.5 EndY=38.25 EndZ=0
    g29: LineSegment StartX=-10.5 StartY=38.25 StartZ=0 EndX=-10.5 EndY=14.2215 EndZ=0
    g30: LineSegment StartX=10.5 StartY=-38.25 StartZ=0 EndX=10.5 EndY=-10.6948 EndZ=0
    g31: LineSegment StartX=-10.5 StartY=-10.6948 StartZ=0 EndX=-10.5 EndY=-38.25 EndZ=0
    g32: ArcOfCircle CenterX=-10.25 CenterY=38.25 CenterZ=0 NormalX=0 NormalY=0 NormalZ=1 AngleXU=0 Radius=0.25 StartAngle=1.5708 EndAngle=3.14159
  constraints (85):
    c: Radius(g1) = 2.2  'Hole Clearance'
    c: Equal(g1,g0)
    c: Equal(g2,g3)
    c: Coincident(g6,g7)
    c: Coincident(g7,g8)
    c: Coincident(g8,g9)
    c: Coincident(g9,g6)
    c: Equal(g6,g7)
    c: Equal(g6,g8)
    c: Equal(g6,g9)
    c: PointOnObject(g6,g10)
    c: PointOnObject(g7,g10)
    c: PointOnObject(g8,g10)
    c: PointOnObject(g9,g10)
    c: Coincident(g0,g6)
    c: Coincident(g1,g7)
    c: Tangent(g3,g11) = 1.5708
    c: Tangent(g0,g11) = 1.5708
    c: Tangent(g0,g12) = 1.5708
    c: Tangent(g4,g12) = 1.5708
    c: Tangent(g5,g13) = 1.5708
    c: Tangent(g1,g13) = 1.5708
    c: Tangent(g1,g14) = 1.5708
    c: Tangent(g2,g14) = 1.5708
    c: Parallel(g3,g6)
    c: Parallel(g2,g7)
    c: Parallel(g4,g9)
    c: Tangent(g13,g10)
    c: Tangent(g14,g10)
    c: Tangent(g12,g10)
    c: Tangent(g11,g10)
    c: Coincident(g10,g-1)
    c: Vertical(g15)
    c: Distance(g9) = 25
    c: Horizontal(g16)
    c: Vertical(g17)
    c: Horizontal(g18)
    c: Vertical(g19)
    c: Tangent(g19,g20) = 1.5708
    c: Tangent(g18,g20) = 1.5708
    c: Tangent(g18,g21) = 1.5708
    c: Tangent(g17,g21) = 1.5708
    c: Tangent(g17,g22) = 1.5708
    c: Tangent(g16,g22) = 1.5708
    c: DistanceX(g19,g17) = 21
    c: Distance(g19,g-2) = 10.5
    c: Parallel(g24,g2)
    c: Perpendicular(g23,g2)
    c: Tangent(g24,g25) = 1.5708
    c: Tangent(g23,g25) = 1.5708
    c: Coincident(g26,g14)
    c: Tangent(g23,g27) = -1.5708
    c: Tangent(g26,g27) = 1.5708
    c: Radius(g25) = 1
    c: Equal(g25,g27)
    c: PointOnObject(g24,g10)
    c: PointOnObject(g24,g10)
    c: PointOnObject(g26,g2)
    c: DistanceY(g18,g16) = 77
    c: Radius(g20) = 0.25
    c: Equal(g20,g21)
    c: Equal(g20,g22)
    c: DistanceY(g18,g-1) = 38.5
    c: PointOnObject(g3,g17)
    c: PointOnObject(g5,g19)
    c: PointOnObject(g4,g17)
    c: PointOnObject(g24,g19)
    c: Equal(g4,g3)
    c: Equal(g3,g5)
    c: Coincident(g8,g15)
    c: Radius(g14) = 1.5
    c: Equal(g14,g13)
    c: Equal(g14,g12)
    c: Coincident(g6,g15)
    c: Coincident(g30,g21)
    c: Coincident(g31,g5)
    c: Coincident(g31,g20)
    c: Coincident(g30,g4)
    c: Coincident(g29,g24)
    c: Coincident(g28,g3)
    c: Coincident(g28,g22)
    c: Tangent(g16,g32) = 1.5708
    c: Tangent(g29,g32) = -1.5708
    c: Coincident(g29,g19)
    c: Radius(g32) = 0.25
FEATURE [PartDesign::Pocket] Pocket
  BaseFeature = -> Pad
  Length = 10
  Length2 = 100
  Profile = -> Sketch002
  Reversed = true
  Type = 0
FEATURE [PartDesign::Body] Body  label="Frame"
  Group = -> [Sketch,Pad,Sketch001,Sketch002,Pocket]
  Origin = -> Origin
  Tip = -> Pocket
FEATURE [Sketcher::SketchObject] Sketch007
  FullyConstrained = true
  MapMode = 5
  Support = -> [XY_Plane001]
  sketch-geometry (8):
    g0: LineSegment StartX=-9 StartY=30 StartZ=0 EndX=9 EndY=30 EndZ=0
    g1: LineSegment StartX=12 StartY=27 StartZ=0 EndX=12 EndY=0 EndZ=0
    g2: LineSegment StartX=12 StartY=0 StartZ=0 EndX=-12 EndY=0 EndZ=0
    g3: LineSegment StartX=-12 StartY=0 StartZ=0 EndX=-12 EndY=27 EndZ=0
    g4: Circle CenterX=-9 CenterY=26 CenterZ=0 NormalX=0 NormalY=0 NormalZ=1 AngleXU=0 Radius=1.5
    g5: Circle CenterX=9 CenterY=26 CenterZ=0 NormalX=0 NormalY=0 NormalZ=1 AngleXU=0 Radius=1.5
    g6: ArcOfCircle CenterX=-9 CenterY=27 CenterZ=0 NormalX=0 NormalY=0 NormalZ=1 AngleXU=0 Radius=3 StartAngle=1.5708 EndAngle=3.14159
    g7: ArcOfCircle CenterX=9 CenterY=27 CenterZ=0 NormalX=0 NormalY=0 NormalZ=1 AngleXU=0 Radius=3 StartAngle=-9e-16 EndAngle=1.5708
  constraints (22):
    c: Horizontal(g0)
    c: Horizontal(g2)
    c: Vertical(g1)
    c: Vertical(g3)
    c: Horizontal(g4,g5)
    c: DistanceX(g4,g5) = 18
    c: Coincident(g2,g1)
    c: Coincident(g2,g3)
    c: Distance(g5,g-2) = 9
    c: DistanceX(g2,g-1) = 12
    c: DistanceX(g-1,g1) = 12
    c: Distance(g5,g0) = 4
    c: Radius(g5) = 1.5
    c: Equal(g5,g4)
    c: PointOnObject(g-1,g2)
    c: Tangent(g0,g6) = 1.5708
    c: Tangent(g3,g6) = 1.5708
    c: Tangent(g0,g7) = 1.5708
    c: Tangent(g1,g7) = 1.5708
    c: Radius(g7) = 3
    c: Equal(g7,g6)
    c: DistanceY(g2,g0) = 30
FEATURE [PartDesign::Pad] Pad001  label="CameraBase"
  Direction = (1,1,1)
  Length = 2
  Length2 = 100
  Profile = -> Sketch007
  Type = 0
FEATURE [Sketcher::SketchObject] Sketch008  label="BaseOfMount"
  FullyConstrained = true
  MapMode = 5
  Placement = pos=(0,0,2) rot=(0,0,1;0rad)
  Support = -> [Pad001]
  sketch-geometry (4):
    g0: LineSegment StartX=-10 StartY=8 StartZ=0 EndX=10 EndY=8 EndZ=0
    g1: LineSegment StartX=10 StartY=8 StartZ=0 EndX=10 EndY=18 EndZ=0
    g2: LineSegment StartX=10 StartY=18 StartZ=0 EndX=-10 EndY=18 EndZ=0
    g3: LineSegment StartX=-10 StartY=18 StartZ=0 EndX=-10 EndY=8 EndZ=0
  constraints (12):
    c: Coincident(g0,g1)
    c: Coincident(g1,g2)
    c: Coincident(g2,g3)
    c: Coincident(g3,g0)
    c: Horizontal(g0)
    c: Horizontal(g2)
    c: Vertical(g1)
    c: Vertical(g3)
    c: Distance(g2,g-1) = 18
    c: Distance(g0,g-2) = 10
    c: Distance(g0,g-2) = 10
    c: DistanceY(g0,g1) = 10
FEATURE [Sketcher::SketchObject] Sketch009  label="TopOfMount"
  AttachmentOffset = pos=(0,0,20) rot=(0,0,1;0rad)
  ExternalGeometry = -> [Sketch008]
  FullyConstrained = true
  MapMode = 5
  Placement = pos=(0,0,22) rot=(0,0,1;0rad)
  Support = -> [Pad001]
  sketch-geometry (4):
    g0: LineSegment StartX=-10 StartY=1 StartZ=0 EndX=10 EndY=1 EndZ=0
    g1: LineSegment StartX=10 StartY=1 StartZ=0 EndX=10 EndY=11 EndZ=0
    g2: LineSegment StartX=10 StartY=11 StartZ=0 EndX=-10 EndY=11 EndZ=0
    g3: LineSegment StartX=-10 StartY=11 StartZ=0 EndX=-10 EndY=1 EndZ=0
  constraints (12):
    c: Coincident(g0,g1)
    c: Coincident(g1,g2)
    c: Coincident(g2,g3)
    c: Coincident(g3,g0)
    c: Horizontal(g2)
    c: Vertical(g1)
    c: Vertical(g3)
    c: Distance(g2,g0) = 10
    c: Horizontal(g0)
    c: PointOnObject(g2,g-4)
    c: PointOnObject(g1,g-5)
    c: Distance(g-5,g2) = 7
FEATURE [PartDesign::AdditiveLoft] AdditiveLoft
  BaseFeature = -> Pad001
  Closed = false
  Profile = -> Sketch008
  Ruled = false
  Sections = -> [Sketch009]
FEATURE [Sketcher::SketchObject] Sketch010
  ExternalGeometry = -> [AdditiveLoft]
  FullyConstrained = true
  MapMode = 5
  Placement = pos=(0,16.6592,5.83073) rot=(0,0.57864,0.815583;3.14159rad)
  Support = -> [AdditiveLoft]
  sketch-geometry (4):
    g0: LineSegment StartX=-7.5 StartY=0.631029 StartZ=0 EndX=7.5 EndY=0.631029 EndZ=0
    g1: LineSegment StartX=7.5 StartY=0.631029 StartZ=0 EndX=7.5 EndY=15.631 EndZ=0
    g2: LineSegment StartX=7.5 StartY=15.631 StartZ=0 EndX=-7.5 EndY=15.631 EndZ=0
    g3: LineSegment StartX=-7.5 StartY=15.631 StartZ=0 EndX=-7.5 EndY=0.631029 EndZ=0
  constraints (12):
    c: Coincident(g0,g1)
    c: Coincident(g1,g2)
    c: Coincident(g2,g3)
    c: Coincident(g3,g0)
    c: Horizontal(g0)
    c: Horizontal(g2)
    c: Vertical(g1)
    c: Vertical(g3)
    c: DistanceY(g3,g3) = 15
    c: DistanceX(g0,g0) = 15
    c: Distance(g2,g-3) = 1.5
    c: Distance(g1,g-2) = 7.5
FEATURE [PartDesign::Pocket] Pocket001
  BaseFeature = -> AdditiveLoft
  Length = 1
  Length2 = 100
  Profile = -> Sketch010
  Type = 0
FEATURE [Sketcher::SketchObject] Sketch011
  ExternalGeometry = -> [Pocket001]
  FullyConstrained = true
  MapMode = 5
  Placement = pos=(0,15.7154,5.50038) rot=(0,0.57864,0.815583;3.14159rad)
  Support = -> [Pocket001]
  sketch-geometry (4):
    g0: Circle CenterX=5.65685 CenterY=13.7879 CenterZ=0 NormalX=0 NormalY=0 NormalZ=1 AngleXU=0 Radius=0.5
    g1: Circle CenterX=-5.65685 CenterY=2.47417 CenterZ=0 NormalX=0 NormalY=0 NormalZ=1 AngleXU=0 Radius=0.5
    g2: Circle CenterX=0 CenterY=8.13103 CenterZ=0 NormalX=0 NormalY=0 NormalZ=1 AngleXU=0 Radius=3.75
    g3: LineSegment StartX=7.5 StartY=15.631 StartZ=0 EndX=-7.5 EndY=0.631029 EndZ=0
  constraints (11):
    c: Diameter(g2) = 7.5
    c: Diameter(g0) = 1
    c: Diameter(g1) = 1
    c: PointOnObject(g2,g-2)
    c: Coincident(g3,g-5)
    c: Coincident(g3,g-6)
    c: PointOnObject(g0,g3)
    c: PointOnObject(g1,g3)
    c: PointOnObject(g2,g3)
    c: Distance(g2,g0) = 8
    c: Distance(g1,g2) = 8
FEATURE [PartDesign::Pocket] Pocket002
  BaseFeature = -> Pocket001
  Length = 10
  Length2 = 100
  Profile = -> Sketch011
  Type = 0
FEATURE [Sketcher::SketchObject] Sketch012
  ExternalGeometry = -> [Pocket002]
  FullyConstrained = true
  MapMode = 5
  Placement = pos=(0,7.75056,2.71269) rot=(1,0,0;1.90747rad)
  Support = -> [Pocket002]
  sketch-geometry (4):
    g0: LineSegment StartX=-7.5 StartY=15.4345 StartZ=0 EndX=7.5 EndY=15.4345 EndZ=0
    g1: LineSegment StartX=7.5 StartY=15.4345 StartZ=0 EndX=7.5 EndY=0.434533 EndZ=0
    g2: LineSegment StartX=7.5 StartY=0.434533 StartZ=0 EndX=-7.5 EndY=0.434533 EndZ=0
    g3: LineSegment StartX=-7.5 StartY=0.434533 StartZ=0 EndX=-7.5 EndY=15.4345 EndZ=0
  constraints (12):
    c: Coincident(g0,g1)
    c: Coincident(g1,g2)
    c: Coincident(g2,g3)
    c: Coincident(g3,g0)
    c: Horizontal(g0)
    c: Horizontal(g2)
    c: Vertical(g1)
    c: Vertical(g3)
    c: DistanceX(g0,g0) = 15
    c: DistanceY(g3,g3) = 15
    c: Distance(g0,g-2) = 7.5
    c: Distance(g0,g-3) = 5
FEATURE [PartDesign::Pocket] Pocket003
  BaseFeature = -> Pocket002
  Length = 7
  Length2 = 100
  Profile = -> Sketch012
  Type = 0
FEATURE [Sketcher::SketchObject] Sketch013
  ExternalGeometry = -> [Pocket003]
  FullyConstrained = true
  MapMode = 5
  Placement = pos=(0,0,22) rot=(0,0,1;0rad)
  Support = -> [Pocket003]
  sketch-geometry (1):
    g0: Circle CenterX=-4.5 CenterY=6.5 CenterZ=0 NormalX=0 NormalY=0 NormalZ=1 AngleXU=0 Radius=3
  constraints (3):
    c: Diameter(g0) = 6
    c: Distance(g0,g-4) = 5.5
    c: Distance(g0,g-3) = 5.5
FEATURE [PartDesign::Pocket] Pocket004
  BaseFeature = -> Pocket003
  Length = 5
  Length2 = 100
  Profile = -> Sketch013
  Type = 0
FEATURE [PartDesign::Body] Body001  label="CameraMount"
  Group = -> [Sketch007,Pad001,Sketch008,Sketch009,AdditiveLoft,Sketch010,Pocket001,Sketch011,Pocket002,Sketch012,Pocket003,Sketch013,Pocket004]
  Origin = -> Origin001
  Tip = -> Pocket004
